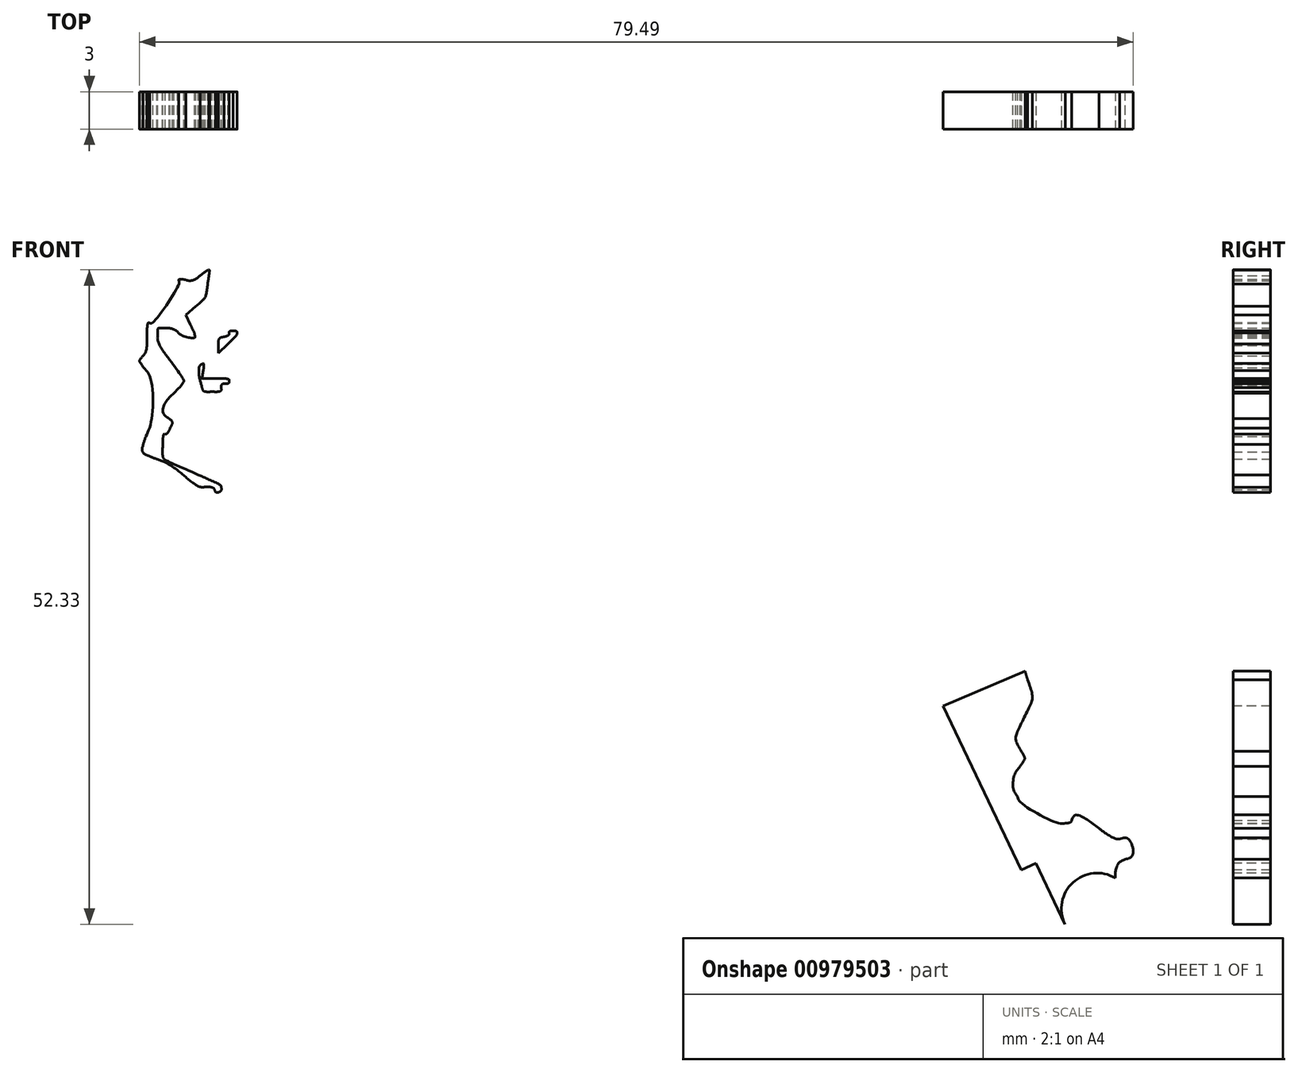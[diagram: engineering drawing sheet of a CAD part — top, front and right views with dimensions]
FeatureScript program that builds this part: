
annotation { "Feature Type Name" : "Feature", "Feature Type Description" : "" }
export const myFeature = defineFeature(function(context is Context, id is Id, definition is map)
    precondition{}
    {
        {
            var Q0;
            Q0=qCreatedBy(makeId("Front.planeOp"),FACE);
            var sketch = newSketch(context, id + "F0", { "sketchPlane" : qUnion([Q0])});
            skLineSegment(sketch, "E0", {"start": v(-32.88, 19.2) * mm, "end": v(-32.1, 20.83) * mm});
            skLineSegment(sketch, "E1", {"start": v(-32.1, 20.83) * mm, "end": v(-32.57, 22.16) * mm});
            skLineSegment(sketch, "E2", {"start": v(-27.5, 16.63) * mm, "end": v(-26.83, 16.28) * mm});
            skLineSegment(sketch, "E3", {"start": v(-26.83, 16.28) * mm, "end": v(-26.97, 16.83) * mm});
            skLineSegment(sketch, "E4", {"start": v(-24.85, 15.67) * mm, "end": v(-25.4, 15.88) * mm});
            skLineSegment(sketch, "E5", {"start": v(-25.4, 15.88) * mm, "end": v(-25.34, 18.4) * mm});
            skLineSegment(sketch, "E6", {"start": v(-1.75, 78.04) * mm, "end": v(-0.2, 79.6) * mm});
            skLineSegment(sketch, "E7", {"start": v(-0.2, 79.6) * mm, "end": v(1.27, 79.6) * mm});
            skLineSegment(sketch, "E8", {"start": v(38.3, 44.26) * mm, "end": v(38.3, 43.17) * mm});
            skLineSegment(sketch, "E9", {"start": v(38.3, 43.17) * mm, "end": v(37.62, 43.24) * mm});
            skLineSegment(sketch, "E10", {"start": v(39.65, -31.25) * mm, "end": v(39.52, -33.83) * mm});
            skLineSegment(sketch, "E11", {"start": v(39.52, -33.83) * mm, "end": v(40.18, -34.42) * mm});
            skLineSegment(sketch, "E12", {"start": v(1.4, 79.08) * mm, "end": v(0.3, 79.22) * mm});
            skLineSegment(sketch, "E13", {"start": v(0.3, 79.22) * mm, "end": v(-1.23, 77.67) * mm});
            skLineSegment(sketch, "E14", {"start": v(-12.51, 69.45) * mm, "end": v(-13.4, 69.45) * mm});
            skLineSegment(sketch, "E15", {"start": v(-13.4, 69.45) * mm, "end": v(-13.27, 67.07) * mm});
            skLineSegment(sketch, "E16", {"start": v(-18.31, 54.9) * mm, "end": v(-18.88, 53.48) * mm});
            skLineSegment(sketch, "E17", {"start": v(-18.88, 53.48) * mm, "end": v(-18.43, 53.1) * mm});
            skLineSegment(sketch, "E18", {"start": v(-20.94, 40.45) * mm, "end": v(-21.55, 40.45) * mm});
            skLineSegment(sketch, "E19", {"start": v(-21.55, 40.45) * mm, "end": v(-21.44, 41.8) * mm});
            skLineSegment(sketch, "E20", {"start": v(-24.47, 43.3) * mm, "end": v(-25.23, 42.61) * mm});
            skLineSegment(sketch, "E21", {"start": v(-25.23, 42.61) * mm, "end": v(-24.8, 41.05) * mm});
            skLineSegment(sketch, "E22", {"start": v(-37.96, -16.18) * mm, "end": v(-37.29, -17.23) * mm});
            skLineSegment(sketch, "E23", {"start": v(-37.29, -17.23) * mm, "end": v(-37.41, -20.41) * mm});
            skLineSegment(sketch, "E24", {"start": v(-30.4, -60.92) * mm, "end": v(-31.42, -62.04) * mm});
            skLineSegment(sketch, "E25", {"start": v(-31.42, -62.04) * mm, "end": v(-30.9, -63.02) * mm});
            skLineSegment(sketch, "E26", {"start": v(-36.35, 33.14) * mm, "end": v(-36.7, 33.88) * mm});
            skLineSegment(sketch, "E27", {"start": v(-36.7, 33.88) * mm, "end": v(-35.92, 34.57) * mm});
            skLineSegment(sketch, "E28", {"start": v(-34.09, 31.43) * mm, "end": v(-34.09, 30.84) * mm});
            skLineSegment(sketch, "E29", {"start": v(-34.09, 30.84) * mm, "end": v(-33.35, 31.56) * mm});
            skFitSpline(sketch, "E30", {"points": [v(-13.45, -80.7) * mm, v(-14.26, -80.4) * mm, v(-15.79, -79.86) * mm, v(-16.84, -79.51) * mm]});
            skFitSpline(sketch, "E31", {"points": [v(-16.84, -79.51) * mm, v(-20.43, -78.33) * mm, v(-20.6, -78.25) * mm, v(-21.55, -77.26) * mm]});
            skFitSpline(sketch, "E32", {"points": [v(-21.55, -77.26) * mm, v(-22.07, -76.72) * mm, v(-23.66, -74.52) * mm, v(-25.09, -72.37) * mm]});
            skFitSpline(sketch, "E33", {"points": [v(-25.09, -72.37) * mm, v(-26.52, -70.21) * mm, v(-28.36, -67.6) * mm, v(-29.19, -66.55) * mm]});
            skFitSpline(sketch, "E34", {"points": [v(-29.19, -66.55) * mm, v(-30.6, -64.76) * mm, v(-31.97, -62.53) * mm, v(-31.97, -62.03) * mm]});
            skFitSpline(sketch, "E35", {"points": [v(-31.97, -62.03) * mm, v(-31.97, -61.91) * mm, v(-31.5, -61.27) * mm, v(-30.92, -60.6) * mm]});
            skFitSpline(sketch, "E36", {"points": [v(-30.92, -60.6) * mm, v(-29.85, -59.39) * mm, v(-29, -57.92) * mm, v(-29, -57.28) * mm]});
            skFitSpline(sketch, "E37", {"points": [v(-29, -57.28) * mm, v(-29, -57.08) * mm, v(-29.34, -56.3) * mm, v(-29.75, -55.53) * mm]});
            skFitSpline(sketch, "E38", {"points": [v(-29.75, -55.53) * mm, v(-30.57, -53.98) * mm, v(-30.63, -53.57) * mm, v(-30.2, -52.72) * mm]});
            skFitSpline(sketch, "E39", {"points": [v(-30.2, -52.72) * mm, v(-29.95, -52.26) * mm, v(-29.92, -51.55) * mm, v(-30.04, -49.29) * mm]});
            skFitSpline(sketch, "E40", {"points": [v(-30.04, -49.29) * mm, v(-30.2, -46.13) * mm, v(-30.12, -46.32) * mm, v(-32.34, -43.6) * mm]});
            skFitSpline(sketch, "E41", {"points": [v(-32.34, -43.6) * mm, v(-32.83, -43) * mm, v(-33.38, -42.01) * mm, v(-33.55, -41.42) * mm]});
            skFitSpline(sketch, "E42", {"points": [v(-33.55, -41.42) * mm, v(-33.73, -40.84) * mm, v(-34.2, -39.94) * mm, v(-34.62, -39.44) * mm]});
            skFitSpline(sketch, "E43", {"points": [v(-34.62, -39.44) * mm, v(-36.03, -37.71) * mm, v(-36.52, -35.97) * mm, v(-35.98, -34.56) * mm]});
            skFitSpline(sketch, "E44", {"points": [v(-35.98, -34.56) * mm, v(-35.86, -34.24) * mm, v(-35.38, -33.57) * mm, v(-34.92, -33.07) * mm]});
            skFitSpline(sketch, "E45", {"points": [v(-34.92, -33.07) * mm, v(-33.97, -32.03) * mm, v(-34, -32.17) * mm, v(-34.37, -30.78) * mm]});
            skFitSpline(sketch, "E46", {"points": [v(-34.37, -30.78) * mm, v(-34.75, -29.38) * mm, v(-35.2, -28.53) * mm, v(-36.46, -26.88) * mm]});
            skFitSpline(sketch, "E47", {"points": [v(-36.46, -26.88) * mm, v(-37.04, -26.13) * mm, v(-37.61, -25.27) * mm, v(-37.73, -24.97) * mm]});
            skFitSpline(sketch, "E48", {"points": [v(-37.73, -24.97) * mm, v(-37.97, -24.39) * mm, v(-38.06, -21.07) * mm, v(-37.9, -18.8) * mm]});
            skFitSpline(sketch, "E49", {"points": [v(-37.9, -18.8) * mm, v(-37.82, -17.55) * mm, v(-37.87, -17.35) * mm, v(-38.39, -16.67) * mm]});
            skFitSpline(sketch, "E50", {"points": [v(-38.39, -16.67) * mm, v(-39.51, -15.19) * mm, v(-39.6, -12.77) * mm, v(-38.72, -7.81) * mm]});
            skFitSpline(sketch, "E51", {"points": [v(-38.72, -7.81) * mm, v(-38.24, -5.14) * mm, v(-38.31, -2.1) * mm, v(-38.87, -1) * mm]});
            skFitSpline(sketch, "E52", {"points": [v(-38.87, -1) * mm, v(-39.1, -0.56) * mm, v(-39.11, -0.29) * mm, v(-38.94, 0.17) * mm]});
            skFitSpline(sketch, "E53", {"points": [v(-38.94, 0.17) * mm, v(-38.62, 1) * mm, v(-38.87, 3.38) * mm, v(-39.5, 5.38) * mm]});
            skFitSpline(sketch, "E54", {"points": [v(-39.5, 5.38) * mm, v(-39.78, 6.29) * mm, v(-40.01, 7.26) * mm, v(-40.01, 7.54) * mm]});
            skFitSpline(sketch, "E55", {"points": [v(-40.01, 7.54) * mm, v(-40.01, 7.83) * mm, v(-39.68, 9.05) * mm, v(-39.27, 10.27) * mm]});
            skFitSpline(sketch, "E56", {"points": [v(-39.27, 10.27) * mm, v(-38.41, 12.85) * mm, v(-38.39, 13.06) * mm, v(-38.96, 13.2) * mm]});
            skFitSpline(sketch, "E57", {"points": [v(-38.96, 13.2) * mm, v(-39.71, 13.4) * mm, v(-39.48, 14.32) * mm, v(-38.38, 15.5) * mm]});
            skFitSpline(sketch, "E58", {"points": [v(-38.38, 15.5) * mm, v(-36.83, 17.16) * mm, v(-35.68, 17.57) * mm, v(-34.74, 16.8) * mm]});
            skFitSpline(sketch, "E59", {"points": [v(-34.74, 16.8) * mm, v(-34.08, 16.26) * mm, v(-32.77, 13.22) * mm, v(-32.66, 11.98) * mm]});
            skFitSpline(sketch, "E60", {"points": [v(-32.66, 11.98) * mm, v(-32.55, 10.86) * mm, v(-32.37, 10.61) * mm, v(-31.6, 10.6) * mm]});
            skFitSpline(sketch, "E61", {"points": [v(-31.6, 10.6) * mm, v(-31, 10.6) * mm, v(-30.96, 11.24) * mm, v(-31.55, 11.77) * mm]});
            skFitSpline(sketch, "E62", {"points": [v(-31.55, 11.77) * mm, v(-31.84, 12.03) * mm, v(-31.97, 12.42) * mm, v(-31.97, 13) * mm]});
            skFitSpline(sketch, "E63", {"points": [v(-31.97, 13) * mm, v(-31.97, 14.32) * mm, v(-32.62, 16.12) * mm, v(-33.18, 16.38) * mm]});
            skFitSpline(sketch, "E64", {"points": [v(-33.18, 16.38) * mm, v(-33.86, 16.69) * mm, v(-33.8, 17.27) * mm, v(-32.88, 19.2) * mm]});
            skFitSpline(sketch, "E65", {"points": [v(-32.57, 22.16) * mm, v(-32.82, 22.9) * mm, v(-33.03, 23.65) * mm, v(-33.03, 23.83) * mm]});
            skFitSpline(sketch, "E66", {"points": [v(-33.03, 23.83) * mm, v(-33.03, 24.1) * mm, v(-33.14, 24.14) * mm, v(-33.5, 24.01) * mm]});
            skFitSpline(sketch, "E67", {"points": [v(-33.5, 24.01) * mm, v(-33.77, 23.92) * mm, v(-34.4, 23.84) * mm, v(-34.93, 23.84) * mm]});
            skFitSpline(sketch, "E68", {"points": [v(-34.93, 23.84) * mm, v(-35.84, 23.83) * mm, v(-35.89, 23.86) * mm, v(-35.95, 24.48) * mm]});
            skFitSpline(sketch, "E69", {"points": [v(-35.95, 24.48) * mm, v(-36.05, 25.55) * mm, v(-34.78, 26.27) * mm, v(-32.78, 26.27) * mm]});
            skFitSpline(sketch, "E70", {"points": [v(-32.78, 26.27) * mm, v(-31.93, 26.27) * mm, v(-31.64, 26.16) * mm, v(-31.1, 25.65) * mm]});
            skFitSpline(sketch, "E71", {"points": [v(-31.1, 25.65) * mm, v(-30.75, 25.3) * mm, v(-30.32, 25.08) * mm, v(-30.15, 25.14) * mm]});
            skFitSpline(sketch, "E72", {"points": [v(-30.15, 25.14) * mm, v(-29.7, 25.31) * mm, v(-29.77, 25.47) * mm, v(-30.7, 26.37) * mm]});
            skFitSpline(sketch, "E73", {"points": [v(-30.7, 26.37) * mm, v(-31.5, 27.15) * mm, v(-31.55, 27.27) * mm, v(-31.55, 28.43) * mm]});
            skFitSpline(sketch, "E74", {"points": [v(-31.55, 28.43) * mm, v(-31.55, 29.6) * mm, v(-31.52, 29.65) * mm, v(-31.02, 29.65) * mm]});
            skFitSpline(sketch, "E75", {"points": [v(-31.02, 29.65) * mm, v(-30.7, 29.65) * mm, v(-30.49, 29.53) * mm, v(-30.49, 29.36) * mm]});
            skFitSpline(sketch, "E76", {"points": [v(-30.49, 29.36) * mm, v(-30.49, 28.94) * mm, v(-28.82, 27.75) * mm, v(-28.24, 27.75) * mm]});
            skFitSpline(sketch, "E77", {"points": [v(-28.24, 27.75) * mm, v(-27.83, 27.75) * mm, v(-27.75, 27.6) * mm, v(-27.62, 26.6) * mm]});
            skFitSpline(sketch, "E78", {"points": [v(-27.62, 26.6) * mm, v(-27.46, 25.26) * mm, v(-27.66, 24.55) * mm, v(-28.57, 23.22) * mm]});
            skFitSpline(sketch, "E79", {"points": [v(-28.57, 23.22) * mm, v(-29.21, 22.29) * mm, v(-29.4, 21.61) * mm, v(-29.02, 21.61) * mm]});
            skFitSpline(sketch, "E80", {"points": [v(-29.02, 21.61) * mm, v(-28.66, 21.61) * mm, v(-28.35, 20.18) * mm, v(-28.49, 19.14) * mm]});
            skFitSpline(sketch, "E81", {"points": [v(-28.49, 19.14) * mm, v(-28.66, 17.84) * mm, v(-28.36, 17.07) * mm, v(-27.5, 16.63) * mm]});
            skFitSpline(sketch, "E82", {"points": [v(-26.97, 16.83) * mm, v(-27.1, 17.33) * mm, v(-27.05, 17.38) * mm, v(-26.5, 17.38) * mm]});
            skFitSpline(sketch, "E83", {"points": [v(-26.5, 17.38) * mm, v(-25.81, 17.38) * mm, v(-25.62, 17.08) * mm, v(-25.62, 16.04) * mm]});
            skFitSpline(sketch, "E84", {"points": [v(-25.62, 16.04) * mm, v(-25.62, 15.5) * mm, v(-25.82, 15.19) * mm, v(-26.56, 14.52) * mm]});
            skFitSpline(sketch, "E85", {"points": [v(-26.56, 14.52) * mm, v(-27.09, 14.05) * mm, v(-27.58, 13.4) * mm, v(-27.66, 13.06) * mm]});
            skFitSpline(sketch, "E86", {"points": [v(-27.66, 13.06) * mm, v(-27.79, 12.49) * mm, v(-27.76, 12.45) * mm, v(-27.3, 12.58) * mm]});
            skFitSpline(sketch, "E87", {"points": [v(-27.3, 12.58) * mm, v(-27.01, 12.65) * mm, v(-26.47, 12.72) * mm, v(-26.09, 12.72) * mm]});
            skFitSpline(sketch, "E88", {"points": [v(-26.09, 12.72) * mm, v(-25.47, 12.72) * mm, v(-25.42, 12.76) * mm, v(-25.61, 13.13) * mm]});
            skFitSpline(sketch, "E89", {"points": [v(-25.61, 13.13) * mm, v(-26.02, 13.88) * mm, v(-25.88, 14.6) * mm, v(-25.31, 14.75) * mm]});
            skFitSpline(sketch, "E90", {"points": [v(-25.31, 14.75) * mm, v(-25.03, 14.82) * mm, v(-24.68, 15.01) * mm, v(-24.55, 15.17) * mm]});
            skFitSpline(sketch, "E91", {"points": [v(-24.55, 15.17) * mm, v(-24.35, 15.4) * mm, v(-24.42, 15.5) * mm, v(-24.85, 15.67) * mm]});
            skFitSpline(sketch, "E92", {"points": [v(-25.34, 18.4) * mm, v(-25.28, 20.49) * mm, v(-25.2, 21.05) * mm, v(-24.84, 21.66) * mm]});
            skFitSpline(sketch, "E93", {"points": [v(-24.84, 21.66) * mm, v(-24.6, 22.07) * mm, v(-24.33, 22.91) * mm, v(-24.25, 23.54) * mm]});
            skFitSpline(sketch, "E94", {"points": [v(-24.25, 23.54) * mm, v(-24.05, 24.98) * mm, v(-23.67, 25.42) * mm, v(-22.64, 25.42) * mm]});
            skFitSpline(sketch, "E95", {"points": [v(-22.64, 25.42) * mm, v(-21.97, 25.42) * mm, v(-21.73, 25.28) * mm, v(-21.09, 24.54) * mm]});
            skFitSpline(sketch, "E96", {"points": [v(-21.09, 24.54) * mm, v(-20.67, 24.05) * mm, v(-20.32, 23.55) * mm, v(-20.32, 23.43) * mm]});
            skFitSpline(sketch, "E97", {"points": [v(-20.32, 23.43) * mm, v(-20.3, 22.93) * mm, v(-19.5, 25.15) * mm, v(-19.5, 25.74) * mm]});
            skFitSpline(sketch, "E98", {"points": [v(-19.5, 25.74) * mm, v(-19.48, 26.68) * mm, v(-19.75, 27) * mm, v(-20.27, 26.68) * mm]});
            skFitSpline(sketch, "E99", {"points": [v(-20.27, 26.68) * mm, v(-20.84, 26.32) * mm, v(-23.7, 26.75) * mm, v(-24.99, 27.38) * mm]});
            skFitSpline(sketch, "E100", {"points": [v(-24.99, 27.38) * mm, v(-26.7, 28.23) * mm, v(-27.27, 29.95) * mm, v(-26.55, 32.07) * mm]});
            skFitSpline(sketch, "E101", {"points": [v(-26.55, 32.07) * mm, v(-26.23, 33) * mm, v(-26.23, 33.13) * mm, v(-26.58, 33.9) * mm]});
            skFitSpline(sketch, "E102", {"points": [v(-26.58, 33.9) * mm, v(-27.04, 34.91) * mm, v(-26.9, 36) * mm, v(-26.2, 36.92) * mm]});
            skFitSpline(sketch, "E103", {"points": [v(-26.2, 36.92) * mm, v(-24.96, 38.54) * mm, v(-24.76, 39.42) * mm, v(-25.3, 40.73) * mm]});
            skFitSpline(sketch, "E104", {"points": [v(-25.3, 40.73) * mm, v(-25.48, 41.15) * mm, v(-25.62, 41.87) * mm, v(-25.62, 42.33) * mm]});
            skFitSpline(sketch, "E105", {"points": [v(-25.62, 42.33) * mm, v(-25.62, 43.02) * mm, v(-25.5, 43.25) * mm, v(-24.99, 43.62) * mm]});
            skFitSpline(sketch, "E106", {"points": [v(-24.99, 43.62) * mm, v(-24.64, 43.87) * mm, v(-24.35, 44.26) * mm, v(-24.35, 44.48) * mm]});
            skFitSpline(sketch, "E107", {"points": [v(-24.35, 44.48) * mm, v(-24.35, 45.6) * mm, v(-22.43, 46.16) * mm, v(-21.62, 45.29) * mm]});
            skFitSpline(sketch, "E108", {"points": [v(-21.62, 45.29) * mm, v(-21.1, 44.74) * mm, v(-20.66, 42.78) * mm, v(-20.82, 41.8) * mm]});
            skFitSpline(sketch, "E109", {"points": [v(-20.82, 41.8) * mm, v(-20.95, 40.98) * mm, v(-20.5, 40.8) * mm, v(-20.12, 41.5) * mm]});
            skFitSpline(sketch, "E110", {"points": [v(-20.12, 41.5) * mm, v(-20, 41.74) * mm, v(-19.7, 41.93) * mm, v(-19.48, 41.93) * mm]});
            skFitSpline(sketch, "E111", {"points": [v(-19.48, 41.93) * mm, v(-19.2, 41.93) * mm, v(-19.03, 42.12) * mm, v(-18.95, 42.51) * mm]});
            skFitSpline(sketch, "E112", {"points": [v(-18.95, 42.51) * mm, v(-18.9, 42.83) * mm, v(-18.75, 43.5) * mm, v(-18.63, 44) * mm]});
            skFitSpline(sketch, "E113", {"points": [v(-18.63, 44) * mm, v(-18.15, 46.1) * mm, v(-18.46, 46.83) * mm, v(-19.95, 47.1) * mm]});
            skFitSpline(sketch, "E114", {"points": [v(-19.95, 47.1) * mm, v(-21.37, 47.35) * mm, v(-21.68, 48.31) * mm, v(-21.02, 50.45) * mm]});
            skFitSpline(sketch, "E115", {"points": [v(-21.02, 50.45) * mm, v(-20.67, 51.58) * mm, v(-20.6, 51.66) * mm, v(-20, 51.67) * mm]});
            skFitSpline(sketch, "E116", {"points": [v(-20, 51.67) * mm, v(-19.64, 51.67) * mm, v(-19.17, 51.8) * mm, v(-18.94, 51.97) * mm]});
            skFitSpline(sketch, "E117", {"points": [v(-18.94, 51.97) * mm, v(-18.56, 52.25) * mm, v(-18.55, 52.28) * mm, v(-18.9, 52.67) * mm]});
            skFitSpline(sketch, "E118", {"points": [v(-18.9, 52.67) * mm, v(-19.36, 53.18) * mm, v(-19.37, 53.99) * mm, v(-18.93, 55) * mm]});
            skFitSpline(sketch, "E119", {"points": [v(-18.93, 55) * mm, v(-18.26, 56.57) * mm, v(-18.22, 56.96) * mm, v(-18.55, 58.71) * mm]});
            skFitSpline(sketch, "E120", {"points": [v(-18.55, 58.71) * mm, v(-19.05, 61.35) * mm, v(-18.66, 63.1) * mm, v(-17.57, 63.1) * mm]});
            skFitSpline(sketch, "E121", {"points": [v(-17.57, 63.1) * mm, v(-17.13, 63.1) * mm, v(-16.93, 62.86) * mm, v(-16.62, 61.94) * mm]});
            skFitSpline(sketch, "E122", {"points": [v(-16.62, 61.94) * mm, v(-16.19, 60.62) * mm, v(-15.25, 61.36) * mm, v(-15.25, 63.03) * mm]});
            skFitSpline(sketch, "E123", {"points": [v(-15.25, 63.03) * mm, v(-15.25, 63.72) * mm, v(-15.21, 63.77) * mm, v(-14.72, 63.65) * mm]});
            skFitSpline(sketch, "E124", {"points": [v(-14.72, 63.65) * mm, v(-13.88, 63.44) * mm, v(-13.7, 64.21) * mm, v(-13.86, 67.25) * mm]});
            skFitSpline(sketch, "E125", {"points": [v(-13.86, 67.25) * mm, v(-14.01, 70.15) * mm, v(-14.06, 70.07) * mm, v(-12.21, 70.08) * mm]});
            skFitSpline(sketch, "E126", {"points": [v(-12.21, 70.08) * mm, v(-11.52, 70.08) * mm, v(-11.25, 70.23) * mm, v(-10.4, 71.12) * mm]});
            skFitSpline(sketch, "E127", {"points": [v(-10.4, 71.12) * mm, v(-9.38, 72.18) * mm, v(-9.03, 72.34) * mm, v(-6.52, 72.84) * mm]});
            skFitSpline(sketch, "E128", {"points": [v(-6.52, 72.84) * mm, v(-4.93, 73.15) * mm, v(-4.21, 73.78) * mm, v(-3.7, 75.27) * mm]});
            skFitSpline(sketch, "E129", {"points": [v(-3.7, 75.27) * mm, v(-3.38, 76.2) * mm, v(-2.96, 76.8) * mm, v(-1.75, 78.04) * mm]});
            skFitSpline(sketch, "E130", {"points": [v(1.27, 79.6) * mm, v(2.66, 79.6) * mm, v(2.79, 79.65) * mm, v(3.57, 80.36) * mm]});
            skFitSpline(sketch, "E131", {"points": [v(3.57, 80.36) * mm, v(4.72, 81.4) * mm, v(5.62, 81.51) * mm, v(6.84, 80.8) * mm]});
            skFitSpline(sketch, "E132", {"points": [v(6.84, 80.8) * mm, v(7.4, 80.48) * mm, v(8.11, 80.24) * mm, v(8.56, 80.24) * mm]});
            skFitSpline(sketch, "E133", {"points": [v(8.56, 80.24) * mm, v(9.65, 80.24) * mm, v(10.66, 79.76) * mm, v(12.03, 78.58) * mm]});
            skFitSpline(sketch, "E134", {"points": [v(12.03, 78.58) * mm, v(12.68, 78.02) * mm, v(13.76, 77.21) * mm, v(14.43, 76.8) * mm]});
            skFitSpline(sketch, "E135", {"points": [v(14.43, 76.8) * mm, v(16.07, 75.75) * mm, v(16.3, 75.23) * mm, v(16.26, 72.68) * mm]});
            skFitSpline(sketch, "E136", {"points": [v(16.26, 72.68) * mm, v(16.21, 70.3) * mm, v(16.3, 70.06) * mm, v(17.99, 67.97) * mm]});
            skFitSpline(sketch, "E137", {"points": [v(17.99, 67.97) * mm, v(19.34, 66.28) * mm, v(19.58, 65.73) * mm, v(19.78, 63.84) * mm]});
            skFitSpline(sketch, "E138", {"points": [v(19.78, 63.84) * mm, v(19.97, 61.97) * mm, v(20.1, 61.75) * mm, v(21.2, 61.28) * mm]});
            skFitSpline(sketch, "E139", {"points": [v(21.2, 61.28) * mm, v(21.95, 60.97) * mm, v(22.77, 60.9) * mm, v(25.95, 60.87) * mm]});
            skFitSpline(sketch, "E140", {"points": [v(25.95, 60.87) * mm, v(29.47, 60.83) * mm, v(29.87, 60.8) * mm, v(30.78, 60.35) * mm]});
            skFitSpline(sketch, "E141", {"points": [v(30.78, 60.35) * mm, v(31.33, 60.09) * mm, v(31.82, 59.71) * mm, v(31.88, 59.53) * mm]});
            skFitSpline(sketch, "E142", {"points": [v(31.88, 59.53) * mm, v(32.1, 58.78) * mm, v(32.32, 58.58) * mm, v(33.34, 58.19) * mm]});
            skFitSpline(sketch, "E143", {"points": [v(33.34, 58.19) * mm, v(35, 57.54) * mm, v(35.47, 56.96) * mm, v(35.61, 55.41) * mm]});
            skFitSpline(sketch, "E144", {"points": [v(35.61, 55.41) * mm, v(35.68, 54.7) * mm, v(35.93, 53.67) * mm, v(36.17, 53.15) * mm]});
            skFitSpline(sketch, "E145", {"points": [v(36.17, 53.15) * mm, v(36.4, 52.63) * mm, v(36.6, 51.94) * mm, v(36.6, 51.62) * mm]});
            skFitSpline(sketch, "E146", {"points": [v(36.6, 51.62) * mm, v(36.6, 51.3) * mm, v(36.8, 50.55) * mm, v(37.02, 49.93) * mm]});
            skFitSpline(sketch, "E147", {"points": [v(37.02, 49.93) * mm, v(37.7, 48.08) * mm, v(38.3, 45.42) * mm, v(38.3, 44.26) * mm]});
            skFitSpline(sketch, "E148", {"points": [v(37.62, 43.24) * mm, v(36.87, 43.31) * mm, v(36.86, 43.33) * mm, v(36.05, 46.9) * mm]});
            skFitSpline(sketch, "E149", {"points": [v(36.05, 46.9) * mm, v(35.75, 48.23) * mm, v(35.65, 48.45) * mm, v(35.6, 47.92) * mm]});
            skFitSpline(sketch, "E150", {"points": [v(35.6, 47.92) * mm, v(35.56, 47.55) * mm, v(35.72, 46.61) * mm, v(35.96, 45.84) * mm]});
            skFitSpline(sketch, "E151", {"points": [v(35.96, 45.84) * mm, v(36.2, 45.06) * mm, v(36.4, 44.16) * mm, v(36.4, 43.83) * mm]});
            skFitSpline(sketch, "E152", {"points": [v(36.4, 43.83) * mm, v(36.4, 42.72) * mm, v(36.23, 42.57) * mm, v(35.04, 42.57) * mm]});
            skFitSpline(sketch, "E153", {"points": [v(35.04, 42.57) * mm, v(34.35, 42.57) * mm, v(33.78, 42.44) * mm, v(33.53, 42.23) * mm]});
            skFitSpline(sketch, "E154", {"points": [v(33.53, 42.23) * mm, v(33.14, 41.92) * mm, v(33.15, 41.9) * mm, v(33.78, 42.01) * mm]});
            skFitSpline(sketch, "E155", {"points": [v(33.78, 42.01) * mm, v(34.37, 42.1) * mm, v(34.48, 42.05) * mm, v(34.7, 41.5) * mm]});
            skFitSpline(sketch, "E156", {"points": [v(34.7, 41.5) * mm, v(35.23, 40.23) * mm, v(34.46, 39.89) * mm, v(32.77, 40.66) * mm]});
            skFitSpline(sketch, "E157", {"points": [v(32.77, 40.66) * mm, v(30, 41.91) * mm, v(30.46, 40.26) * mm, v(33.3, 38.77) * mm]});
            skFitSpline(sketch, "E158", {"points": [v(33.3, 38.77) * mm, v(34.7, 38.04) * mm, v(35.03, 37.98) * mm, v(35.2, 38.44) * mm]});
            skFitSpline(sketch, "E159", {"points": [v(35.2, 38.44) * mm, v(35.4, 38.97) * mm, v(36.94, 38.86) * mm, v(37.34, 38.29) * mm]});
            skFitSpline(sketch, "E160", {"points": [v(37.34, 38.29) * mm, v(37.8, 37.64) * mm, v(37.75, 36.5) * mm, v(37.25, 35.69) * mm]});
            skFitSpline(sketch, "E161", {"points": [v(37.25, 35.69) * mm, v(37.01, 35.31) * mm, v(36.68, 34.6) * mm, v(36.5, 34.09) * mm]});
            skFitSpline(sketch, "E162", {"points": [v(36.5, 34.09) * mm, v(36.07, 32.87) * mm, v(35.62, 32.4) * mm, v(34.86, 32.4) * mm]});
            skFitSpline(sketch, "E163", {"points": [v(34.86, 32.4) * mm, v(34.06, 32.4) * mm, v(32.85, 32.98) * mm, v(32.57, 33.5) * mm]});
            skFitSpline(sketch, "E164", {"points": [v(32.57, 33.5) * mm, v(32.35, 33.9) * mm, v(32.37, 33.91) * mm, v(33.4, 34.23) * mm]});
            skFitSpline(sketch, "E165", {"points": [v(33.4, 34.23) * mm, v(33.55, 34.27) * mm, v(33.64, 34.43) * mm, v(33.6, 34.58) * mm]});
            skFitSpline(sketch, "E166", {"points": [v(33.6, 34.58) * mm, v(33.47, 34.97) * mm, v(32.1, 35.02) * mm, v(31.26, 34.66) * mm]});
            skFitSpline(sketch, "E167", {"points": [v(31.26, 34.66) * mm, v(30.63, 34.4) * mm, v(30.54, 34.27) * mm, v(30.63, 33.8) * mm]});
            skFitSpline(sketch, "E168", {"points": [v(30.63, 33.8) * mm, v(30.71, 33.37) * mm, v(30.83, 33.27) * mm, v(31.13, 33.37) * mm]});
            skFitSpline(sketch, "E169", {"points": [v(31.13, 33.37) * mm, v(31.68, 33.54) * mm, v(31.8, 33.13) * mm, v(31.57, 31.7) * mm]});
            skFitSpline(sketch, "E170", {"points": [v(31.57, 31.7) * mm, v(31.47, 31.04) * mm, v(31.4, 30.5) * mm, v(31.43, 30.5) * mm]});
            skFitSpline(sketch, "E171", {"points": [v(31.43, 30.5) * mm, v(31.46, 30.5) * mm, v(31.82, 30.65) * mm, v(32.25, 30.82) * mm]});
            skFitSpline(sketch, "E172", {"points": [v(32.25, 30.82) * mm, v(33.01, 31.14) * mm, v(33.02, 31.14) * mm, v(33.26, 30.56) * mm]});
            skFitSpline(sketch, "E173", {"points": [v(33.26, 30.56) * mm, v(33.39, 30.24) * mm, v(33.5, 29.43) * mm, v(33.52, 28.77) * mm]});
            skFitSpline(sketch, "E174", {"points": [v(33.52, 28.77) * mm, v(33.55, 27.14) * mm, v(33.03, 26.57) * mm, v(31.4, 26.43) * mm]});
            skFitSpline(sketch, "E175", {"points": [v(31.4, 26.43) * mm, v(29.99, 26.32) * mm, v(29.27, 25.83) * mm, v(28.59, 24.5) * mm]});
            skFitSpline(sketch, "E176", {"points": [v(28.59, 24.5) * mm, v(28.09, 23.52) * mm, v(28.09, 23.5) * mm, v(28.46, 22.8) * mm]});
            skFitSpline(sketch, "E177", {"points": [v(28.46, 22.8) * mm, v(29.02, 21.76) * mm, v(28.8, 20.5) * mm, v(27.76, 18.77) * mm]});
            skFitSpline(sketch, "E178", {"points": [v(27.76, 18.77) * mm, v(26.26, 16.28) * mm, v(26.34, 15.6) * mm, v(28.5, 12.89) * mm]});
            skFitSpline(sketch, "E179", {"points": [v(28.5, 12.89) * mm, v(30.07, 10.9) * mm, v(30.64, 9.85) * mm, v(31.32, 7.7) * mm]});
            skFitSpline(sketch, "E180", {"points": [v(31.32, 7.7) * mm, v(31.79, 6.2) * mm, v(31.8, 6.14) * mm, v(31.41, 5.73) * mm]});
            skFitSpline(sketch, "E181", {"points": [v(31.41, 5.73) * mm, v(31.08, 5.36) * mm, v(31.06, 5.2) * mm, v(31.28, 4.6) * mm]});
            skFitSpline(sketch, "E182", {"points": [v(31.28, 4.6) * mm, v(31.65, 3.58) * mm, v(31.59, 2.92) * mm, v(31, 1.59) * mm]});
            skFitSpline(sketch, "E183", {"points": [v(31, 1.59) * mm, v(30.4, 0.22) * mm, v(30.37, 0) * mm, v(30.73, -0.98) * mm]});
            skFitSpline(sketch, "E184", {"points": [v(30.73, -0.98) * mm, v(30.96, -1.6) * mm, v(30.93, -1.79) * mm, v(30.48, -2.62) * mm]});
            skFitSpline(sketch, "E185", {"points": [v(30.48, -2.62) * mm, v(29.76, -3.92) * mm, v(30.03, -4.4) * mm, v(31.97, -5.39) * mm]});
            skFitSpline(sketch, "E186", {"points": [v(31.97, -5.39) * mm, v(33.32, -6.07) * mm, v(33.55, -6.12) * mm, v(34.1, -5.9) * mm]});
            skFitSpline(sketch, "E187", {"points": [v(34.1, -5.9) * mm, v(34.89, -5.57) * mm, v(35.48, -5.74) * mm, v(36.67, -6.64) * mm]});
            skFitSpline(sketch, "E188", {"points": [v(36.67, -6.64) * mm, v(37.21, -7.06) * mm, v(37.94, -7.45) * mm, v(38.28, -7.52) * mm]});
            skFitSpline(sketch, "E189", {"points": [v(38.28, -7.52) * mm, v(38.74, -7.61) * mm, v(38.97, -7.82) * mm, v(39.14, -8.29) * mm]});
            skFitSpline(sketch, "E190", {"points": [v(39.14, -8.29) * mm, v(39.46, -9.22) * mm, v(39.43, -9.36) * mm, v(38.73, -10.24) * mm]});
            skFitSpline(sketch, "E191", {"points": [v(38.73, -10.24) * mm, v(37.95, -11.22) * mm, v(37.9, -12.13) * mm, v(38.57, -13.12) * mm]});
            skFitSpline(sketch, "E192", {"points": [v(38.57, -13.12) * mm, v(38.94, -13.67) * mm, v(39.23, -13.86) * mm, v(39.79, -13.91) * mm]});
            skFitSpline(sketch, "E193", {"points": [v(39.79, -13.91) * mm, v(40.2, -13.95) * mm, v(40.6, -14.1) * mm, v(40.68, -14.23) * mm]});
            skFitSpline(sketch, "E194", {"points": [v(40.68, -14.23) * mm, v(40.98, -14.7) * mm, v(40.84, -15.58) * mm, v(40.4, -15.98) * mm]});
            skFitSpline(sketch, "E195", {"points": [v(40.4, -15.98) * mm, v(40.04, -16.3) * mm, v(39.97, -16.56) * mm, v(40.05, -17.26) * mm]});
            skFitSpline(sketch, "E196", {"points": [v(40.05, -17.26) * mm, v(40.14, -18.03) * mm, v(40.09, -18.17) * mm, v(39.65, -18.37) * mm]});
            skFitSpline(sketch, "E197", {"points": [v(39.65, -18.37) * mm, v(39.06, -18.64) * mm, v(39.03, -18.9) * mm, v(39.5, -20) * mm]});
            skFitSpline(sketch, "E198", {"points": [v(39.5, -20) * mm, v(39.77, -20.67) * mm, v(39.83, -21.57) * mm, v(39.81, -24.74) * mm]});
            skFitSpline(sketch, "E199", {"points": [v(39.81, -24.74) * mm, v(39.8, -26.9) * mm, v(39.73, -29.82) * mm, v(39.65, -31.25) * mm]});
            skFitSpline(sketch, "E200", {"points": [v(40.18, -34.42) * mm, v(40.54, -34.74) * mm, v(40.84, -35.18) * mm, v(40.84, -35.41) * mm]});
            skFitSpline(sketch, "E201", {"points": [v(40.84, -35.41) * mm, v(40.84, -36.27) * mm, v(39.96, -37.65) * mm, v(38.92, -38.41) * mm]});
            skFitSpline(sketch, "E202", {"points": [v(38.92, -38.41) * mm, v(37.63, -39.36) * mm, v(37.28, -40) * mm, v(37.05, -41.89) * mm]});
            skFitSpline(sketch, "E203", {"points": [v(37.05, -41.89) * mm, v(36.94, -42.7) * mm, v(36.66, -43.77) * mm, v(36.42, -44.27) * mm]});
            skFitSpline(sketch, "E204", {"points": [v(36.42, -44.27) * mm, v(35.96, -45.22) * mm, v(33.78, -47.87) * mm, v(31.3, -50.5) * mm]});
            skFitSpline(sketch, "E205", {"points": [v(31.3, -50.5) * mm, v(29.02, -52.92) * mm, v(27.8, -55.66) * mm, v(27.2, -59.77) * mm]});
            skFitSpline(sketch, "E206", {"points": [v(27.2, -59.77) * mm, v(26.85, -62.13) * mm, v(26.75, -62.37) * mm, v(25.14, -65) * mm]});
            skFitSpline(sketch, "E207", {"points": [v(25.14, -65) * mm, v(24.58, -65.91) * mm, v(24.35, -66.6) * mm, v(24.16, -67.9) * mm]});
            skFitSpline(sketch, "E208", {"points": [v(24.16, -67.9) * mm, v(23.88, -69.93) * mm, v(23.36, -71.03) * mm, v(22.29, -71.92) * mm]});
            skFitSpline(sketch, "E209", {"points": [v(22.29, -71.92) * mm, v(21.43, -72.63) * mm, v(19.94, -73.22) * mm, v(19, -73.22) * mm]});
            skFitSpline(sketch, "E210", {"points": [v(19, -73.22) * mm, v(18.6, -73.22) * mm, v(18.4, -73.32) * mm, v(18.4, -73.56) * mm]});
            skFitSpline(sketch, "E211", {"points": [v(18.4, -73.56) * mm, v(18.4, -73.75) * mm, v(18.21, -74.22) * mm, v(17.97, -74.6) * mm]});
            skFitSpline(sketch, "E212", {"points": [v(17.97, -74.6) * mm, v(17.57, -75.26) * mm, v(17.56, -75.35) * mm, v(17.87, -76.08) * mm]});
            skFitSpline(sketch, "E213", {"points": [v(17.87, -76.08) * mm, v(18.34, -77.22) * mm, v(18.3, -77.38) * mm, v(17.14, -78.58) * mm]});
            skFitSpline(sketch, "E214", {"points": [v(17.14, -78.58) * mm, v(16.56, -79.18) * mm, v(15.87, -79.93) * mm, v(15.6, -80.25) * mm]});
            skFitSpline(sketch, "E215", {"points": [v(15.6, -80.25) * mm, v(15.34, -80.56) * mm, v(14.86, -80.88) * mm, v(14.54, -80.96) * mm]});
            skFitSpline(sketch, "E216", {"points": [v(14.54, -80.96) * mm, v(14.03, -81.08) * mm, v(13.96, -81.03) * mm, v(13.96, -80.56) * mm]});
            skFitSpline(sketch, "E217", {"points": [v(13.96, -80.56) * mm, v(13.96, -80.25) * mm, v(13.75, -79.86) * mm, v(13.47, -79.63) * mm]});
            skFitSpline(sketch, "E218", {"points": [v(13.47, -79.63) * mm, v(12.33, -78.73) * mm, v(12.3, -77.45) * mm, v(13.44, -77.45) * mm]});
            skFitSpline(sketch, "E219", {"points": [v(13.44, -77.45) * mm, v(14.2, -77.45) * mm, v(15.11, -76) * mm, v(14.94, -75.07) * mm]});
            skFitSpline(sketch, "E220", {"points": [v(14.94, -75.07) * mm, v(14.87, -74.7) * mm, v(14.75, -74.02) * mm, v(14.67, -73.57) * mm]});
            skFitSpline(sketch, "E221", {"points": [v(14.67, -73.57) * mm, v(14.58, -73.02) * mm, v(14.45, -72.8) * mm, v(14.25, -72.88) * mm]});
            skFitSpline(sketch, "E222", {"points": [v(14.25, -72.88) * mm, v(14.1, -72.94) * mm, v(13.13, -72.88) * mm, v(12.11, -72.76) * mm]});
            skFitSpline(sketch, "E223", {"points": [v(12.11, -72.76) * mm, v(10.8, -72.6) * mm, v(10.12, -72.4) * mm, v(9.8, -72.1) * mm]});
            skFitSpline(sketch, "E224", {"points": [v(9.8, -72.1) * mm, v(9.32, -71.67) * mm, v(8.88, -71.75) * mm, v(8.88, -72.28) * mm]});
            skFitSpline(sketch, "E225", {"points": [v(8.88, -72.28) * mm, v(8.88, -72.66) * mm, v(8.5, -72.65) * mm, v(7.82, -72.26) * mm]});
            skFitSpline(sketch, "E226", {"points": [v(7.82, -72.26) * mm, v(7.11, -71.86) * mm, v(5.83, -71.87) * mm, v(4.94, -72.29) * mm]});
            skFitSpline(sketch, "E227", {"points": [v(4.94, -72.29) * mm, v(4.16, -72.66) * mm, v(4.18, -72.61) * mm, v(4.14, -74.27) * mm]});
            skFitSpline(sketch, "E228", {"points": [v(4.14, -74.27) * mm, v(4.12, -75.43) * mm, v(4.11, -75.44) * mm, v(3.17, -75.91) * mm]});
            skFitSpline(sketch, "E229", {"points": [v(3.17, -75.91) * mm, v(2.65, -76.18) * mm, v(1.84, -76.77) * mm, v(1.36, -77.24) * mm]});
            skFitSpline(sketch, "E230", {"points": [v(1.36, -77.24) * mm, v(0.68, -77.91) * mm, v(-0.19, -78.37) * mm, v(-2.67, -79.37) * mm]});
            skFitSpline(sketch, "E231", {"points": [v(-2.67, -79.37) * mm, v(-6.5, -80.92) * mm, v(-7.82, -81.25) * mm, v(-10.17, -81.25) * mm]});
            skFitSpline(sketch, "E232", {"points": [v(-10.17, -81.25) * mm, v(-11.59, -81.25) * mm, v(-12.28, -81.13) * mm, v(-13.45, -80.7) * mm]});
            skFitSpline(sketch, "E233", {"points": [v(-6.84, -80.3) * mm, v(-6.29, -80.14) * mm, v(-4.56, -79.5) * mm, v(-3, -78.88) * mm]});
            skFitSpline(sketch, "E234", {"points": [v(-3, -78.88) * mm, v(-0.66, -77.96) * mm, v(0.05, -77.57) * mm, v(1.08, -76.65) * mm]});
            skFitSpline(sketch, "E235", {"points": [v(1.08, -76.65) * mm, v(1.77, -76.04) * mm, v(2.46, -75.54) * mm, v(2.62, -75.54) * mm]});
            skFitSpline(sketch, "E236", {"points": [v(2.62, -75.54) * mm, v(2.78, -75.54) * mm, v(3.12, -75.37) * mm, v(3.38, -75.16) * mm]});
            skFitSpline(sketch, "E237", {"points": [v(3.38, -75.16) * mm, v(3.8, -74.81) * mm, v(3.83, -74.72) * mm, v(3.59, -73.93) * mm]});
            skFitSpline(sketch, "E238", {"points": [v(3.59, -73.93) * mm, v(3.4, -73.28) * mm, v(3.39, -72.96) * mm, v(3.57, -72.61) * mm]});
            skFitSpline(sketch, "E239", {"points": [v(3.57, -72.61) * mm, v(4.07, -71.69) * mm, v(6.12, -71.11) * mm, v(7.53, -71.5) * mm]});
            skFitSpline(sketch, "E240", {"points": [v(7.53, -71.5) * mm, v(8.17, -71.68) * mm, v(8.4, -71.66) * mm, v(8.68, -71.41) * mm]});
            skFitSpline(sketch, "E241", {"points": [v(8.68, -71.41) * mm, v(9.15, -70.98) * mm, v(9.64, -71.02) * mm, v(10.13, -71.54) * mm]});
            skFitSpline(sketch, "E242", {"points": [v(10.13, -71.54) * mm, v(10.44, -71.88) * mm, v(10.95, -72.03) * mm, v(12.2, -72.17) * mm]});
            skFitSpline(sketch, "E243", {"points": [v(12.2, -72.17) * mm, v(13.1, -72.28) * mm, v(14, -72.32) * mm, v(14.17, -72.26) * mm]});
            skFitSpline(sketch, "E244", {"points": [v(14.17, -72.26) * mm, v(14.75, -72.09) * mm, v(15.04, -72.5) * mm, v(15.33, -73.91) * mm]});
            skFitSpline(sketch, "E245", {"points": [v(15.33, -73.91) * mm, v(15.54, -74.89) * mm, v(15.57, -75.53) * mm, v(15.43, -76.04) * mm]});
            skFitSpline(sketch, "E246", {"points": [v(15.43, -76.04) * mm, v(15.14, -77.06) * mm, v(14.45, -77.87) * mm, v(13.85, -77.87) * mm]});
            skFitSpline(sketch, "E247", {"points": [v(13.85, -77.87) * mm, v(13.06, -77.87) * mm, v(13.01, -78.27) * mm, v(13.7, -79) * mm]});
            skFitSpline(sketch, "E248", {"points": [v(13.7, -79) * mm, v(14.06, -79.37) * mm, v(14.38, -79.86) * mm, v(14.43, -80.1) * mm]});
            skFitSpline(sketch, "E249", {"points": [v(14.43, -80.1) * mm, v(14.5, -80.48) * mm, v(14.55, -80.47) * mm, v(15.03, -79.9) * mm]});
            skFitSpline(sketch, "E250", {"points": [v(15.03, -79.9) * mm, v(15.31, -79.57) * mm, v(16.02, -78.83) * mm, v(16.6, -78.28) * mm]});
            skFitSpline(sketch, "E251", {"points": [v(16.6, -78.28) * mm, v(17.64, -77.28) * mm, v(17.65, -77.26) * mm, v(17.4, -76.55) * mm]});
            skFitSpline(sketch, "E252", {"points": [v(17.4, -76.55) * mm, v(17.05, -75.6) * mm, v(17.07, -74.87) * mm, v(17.45, -74.37) * mm]});
            skFitSpline(sketch, "E253", {"points": [v(17.45, -74.37) * mm, v(17.62, -74.14) * mm, v(17.76, -73.7) * mm, v(17.76, -73.4) * mm]});
            skFitSpline(sketch, "E254", {"points": [v(17.76, -73.4) * mm, v(17.77, -72.89) * mm, v(17.86, -72.83) * mm, v(18.88, -72.7) * mm]});
            skFitSpline(sketch, "E255", {"points": [v(18.88, -72.7) * mm, v(19.5, -72.62) * mm, v(20.47, -72.3) * mm, v(21.04, -71.99) * mm]});
            skFitSpline(sketch, "E256", {"points": [v(21.04, -71.99) * mm, v(22.45, -71.22) * mm, v(23.22, -70.08) * mm, v(23.5, -68.35) * mm]});
            skFitSpline(sketch, "E257", {"points": [v(23.5, -68.35) * mm, v(23.9, -65.9) * mm, v(24.16, -65.2) * mm, v(25.1, -63.87) * mm]});
            skFitSpline(sketch, "E258", {"points": [v(25.1, -63.87) * mm, v(26.18, -62.33) * mm, v(26.35, -61.85) * mm, v(26.67, -59.46) * mm]});
            skFitSpline(sketch, "E259", {"points": [v(26.67, -59.46) * mm, v(26.98, -57.13) * mm, v(27.93, -54.18) * mm, v(28.89, -52.58) * mm]});
            skFitSpline(sketch, "E260", {"points": [v(28.89, -52.58) * mm, v(29.3, -51.88) * mm, v(30.25, -50.69) * mm, v(31, -49.93) * mm]});
            skFitSpline(sketch, "E261", {"points": [v(31, -49.93) * mm, v(33.26, -47.61) * mm, v(35.36, -45.01) * mm, v(35.9, -43.88) * mm]});
            skFitSpline(sketch, "E262", {"points": [v(35.9, -43.88) * mm, v(36.17, -43.28) * mm, v(36.49, -42.11) * mm, v(36.6, -41.27) * mm]});
            skFitSpline(sketch, "E263", {"points": [v(36.6, -41.27) * mm, v(36.81, -39.5) * mm, v(37.06, -39.06) * mm, v(38.37, -38.07) * mm]});
            skFitSpline(sketch, "E264", {"points": [v(38.37, -38.07) * mm, v(39.26, -37.4) * mm, v(40.2, -36.1) * mm, v(40.2, -35.57) * mm]});
            skFitSpline(sketch, "E265", {"points": [v(40.2, -35.57) * mm, v(40.2, -35.45) * mm, v(39.98, -35.11) * mm, v(39.7, -34.83) * mm]});
            skFitSpline(sketch, "E266", {"points": [v(39.7, -34.83) * mm, v(38.98, -34.12) * mm, v(38.86, -33.18) * mm, v(39.13, -30.68) * mm]});
            skFitSpline(sketch, "E267", {"points": [v(39.13, -30.68) * mm, v(39.26, -29.5) * mm, v(39.36, -26.93) * mm, v(39.36, -24.95) * mm]});
            skFitSpline(sketch, "E268", {"points": [v(39.36, -24.95) * mm, v(39.36, -21.87) * mm, v(39.3, -21.22) * mm, v(38.94, -20.3) * mm]});
            skFitSpline(sketch, "E269", {"points": [v(38.94, -20.3) * mm, v(38.39, -18.9) * mm, v(38.4, -18.51) * mm, v(39.04, -18) * mm]});
            skFitSpline(sketch, "E270", {"points": [v(39.04, -18) * mm, v(39.45, -17.69) * mm, v(39.57, -17.4) * mm, v(39.57, -16.76) * mm]});
            skFitSpline(sketch, "E271", {"points": [v(39.57, -16.76) * mm, v(39.57, -16.2) * mm, v(39.7, -15.8) * mm, v(39.97, -15.56) * mm]});
            skFitSpline(sketch, "E272", {"points": [v(39.97, -15.56) * mm, v(40.59, -15) * mm, v(40.32, -14.37) * mm, v(39.46, -14.37) * mm]});
            skFitSpline(sketch, "E273", {"points": [v(39.46, -14.37) * mm, v(38.38, -14.37) * mm, v(37.67, -13.4) * mm, v(37.67, -11.9) * mm]});
            skFitSpline(sketch, "E274", {"points": [v(37.67, -11.9) * mm, v(37.67, -10.72) * mm, v(37.93, -9.95) * mm, v(38.44, -9.65) * mm]});
            skFitSpline(sketch, "E275", {"points": [v(38.44, -9.65) * mm, v(39.04, -9.3) * mm, v(38.7, -8.02) * mm, v(38, -8.02) * mm]});
            skFitSpline(sketch, "E276", {"points": [v(38, -8.02) * mm, v(37.74, -8.02) * mm, v(37, -7.64) * mm, v(36.34, -7.18) * mm]});
            skFitSpline(sketch, "E277", {"points": [v(36.34, -7.18) * mm, v(35.18, -6.34) * mm, v(34.43, -6.12) * mm, v(34.18, -6.54) * mm]});
            skFitSpline(sketch, "E278", {"points": [v(34.18, -6.54) * mm, v(34.1, -6.66) * mm, v(33.87, -6.75) * mm, v(33.65, -6.75) * mm]});
            skFitSpline(sketch, "E279", {"points": [v(33.65, -6.75) * mm, v(33.07, -6.75) * mm, v(30.08, -5.09) * mm, v(29.83, -4.63) * mm]});
            skFitSpline(sketch, "E280", {"points": [v(29.83, -4.63) * mm, v(29.5, -4) * mm, v(29.6, -2.89) * mm, v(30.04, -2.22) * mm]});
            skFitSpline(sketch, "E281", {"points": [v(30.04, -2.22) * mm, v(30.4, -1.66) * mm, v(30.41, -1.54) * mm, v(30.14, -1.01) * mm]});
            skFitSpline(sketch, "E282", {"points": [v(30.14, -1.01) * mm, v(29.71, -0.19) * mm, v(29.76, 0.38) * mm, v(30.37, 1.68) * mm]});
            skFitSpline(sketch, "E283", {"points": [v(30.37, 1.68) * mm, v(30.96, 2.95) * mm, v(31, 3.5) * mm, v(30.65, 4.7) * mm]});
            skFitSpline(sketch, "E284", {"points": [v(30.65, 4.7) * mm, v(30.44, 5.4) * mm, v(30.46, 5.58) * mm, v(30.78, 5.93) * mm]});
            skFitSpline(sketch, "E285", {"points": [v(30.78, 5.93) * mm, v(31.13, 6.33) * mm, v(31.13, 6.4) * mm, v(30.68, 7.79) * mm]});
            skFitSpline(sketch, "E286", {"points": [v(30.68, 7.79) * mm, v(30.01, 9.8) * mm, v(29.64, 10.47) * mm, v(28.1, 12.43) * mm]});
            skFitSpline(sketch, "E287", {"points": [v(28.1, 12.43) * mm, v(27.35, 13.37) * mm, v(26.61, 14.44) * mm, v(26.46, 14.8) * mm]});
            skFitSpline(sketch, "E288", {"points": [v(26.46, 14.8) * mm, v(26, 15.95) * mm, v(26.28, 17.5) * mm, v(27.26, 19.16) * mm]});
            skFitSpline(sketch, "E289", {"points": [v(27.26, 19.16) * mm, v(28.4, 21.1) * mm, v(28.53, 21.7) * mm, v(27.93, 22.5) * mm]});
            skFitSpline(sketch, "E290", {"points": [v(27.93, 22.5) * mm, v(27.4, 23.23) * mm, v(27.46, 23.77) * mm, v(28.28, 25.17) * mm]});
            skFitSpline(sketch, "E291", {"points": [v(28.28, 25.17) * mm, v(28.94, 26.3) * mm, v(29.89, 26.9) * mm, v(31.02, 26.9) * mm]});
            skFitSpline(sketch, "E292", {"points": [v(31.02, 26.9) * mm, v(31.6, 26.9) * mm, v(32.1, 27.06) * mm, v(32.48, 27.36) * mm]});
            skFitSpline(sketch, "E293", {"points": [v(32.48, 27.36) * mm, v(33, 27.78) * mm, v(33.05, 27.91) * mm, v(32.96, 28.95) * mm]});
            skFitSpline(sketch, "E294", {"points": [v(32.96, 28.95) * mm, v(32.91, 29.57) * mm, v(32.82, 30.13) * mm, v(32.76, 30.19) * mm]});
            skFitSpline(sketch, "E295", {"points": [v(32.76, 30.19) * mm, v(32.7, 30.25) * mm, v(32.3, 30.15) * mm, v(31.89, 29.97) * mm]});
            skFitSpline(sketch, "E296", {"points": [v(31.89, 29.97) * mm, v(31.46, 29.8) * mm, v(31.06, 29.65) * mm, v(30.98, 29.65) * mm]});
            skFitSpline(sketch, "E297", {"points": [v(30.98, 29.65) * mm, v(30.9, 29.65) * mm, v(30.9, 30.37) * mm, v(30.97, 31.24) * mm]});
            skFitSpline(sketch, "E298", {"points": [v(30.97, 31.24) * mm, v(31.1, 32.73) * mm, v(31.07, 32.83) * mm, v(30.68, 32.83) * mm]});
            skFitSpline(sketch, "E299", {"points": [v(30.68, 32.83) * mm, v(30.45, 32.83) * mm, v(30.26, 32.97) * mm, v(30.26, 33.15) * mm]});
            skFitSpline(sketch, "E300", {"points": [v(30.26, 33.15) * mm, v(30.26, 33.32) * mm, v(30.16, 33.46) * mm, v(30.05, 33.46) * mm]});
            skFitSpline(sketch, "E301", {"points": [v(30.05, 33.46) * mm, v(29.69, 33.46) * mm, v(29.82, 34.44) * mm, v(30.23, 34.81) * mm]});
            skFitSpline(sketch, "E302", {"points": [v(30.23, 34.81) * mm, v(30.44, 35) * mm, v(31.16, 35.28) * mm, v(31.83, 35.42) * mm]});
            skFitSpline(sketch, "E303", {"points": [v(31.83, 35.42) * mm, v(32.85, 35.63) * mm, v(33.13, 35.62) * mm, v(33.6, 35.36) * mm]});
            skFitSpline(sketch, "E304", {"points": [v(33.6, 35.36) * mm, v(34.37, 34.93) * mm, v(34.48, 34.05) * mm, v(33.82, 33.73) * mm]});
            skFitSpline(sketch, "E305", {"points": [v(33.82, 33.73) * mm, v(33.34, 33.51) * mm, v(33.35, 33.5) * mm, v(34.15, 33.16) * mm]});
            skFitSpline(sketch, "E306", {"points": [v(34.15, 33.16) * mm, v(34.9, 32.83) * mm, v(34.99, 32.83) * mm, v(35.36, 33.17) * mm]});
            skFitSpline(sketch, "E307", {"points": [v(35.36, 33.17) * mm, v(35.58, 33.37) * mm, v(35.76, 33.64) * mm, v(35.76, 33.77) * mm]});
            skFitSpline(sketch, "E308", {"points": [v(35.76, 33.77) * mm, v(35.76, 33.9) * mm, v(36.1, 34.7) * mm, v(36.5, 35.56) * mm]});
            skFitSpline(sketch, "E309", {"points": [v(36.5, 35.56) * mm, v(37.29, 37.18) * mm, v(37.3, 37.75) * mm, v(36.61, 38.12) * mm]});
            skFitSpline(sketch, "E310", {"points": [v(36.61, 38.12) * mm, v(36.14, 38.38) * mm, v(35.55, 38.19) * mm, v(35.55, 37.78) * mm]});
            skFitSpline(sketch, "E311", {"points": [v(35.55, 37.78) * mm, v(35.55, 36.66) * mm, v(30.79, 39.12) * mm, v(30.36, 40.45) * mm]});
            skFitSpline(sketch, "E312", {"points": [v(30.36, 40.45) * mm, v(30.3, 40.68) * mm, v(30.34, 41.05) * mm, v(30.47, 41.29) * mm]});
            skFitSpline(sketch, "E313", {"points": [v(30.47, 41.29) * mm, v(30.77, 41.86) * mm, v(31.55, 41.83) * mm, v(33.01, 41.2) * mm]});
            skFitSpline(sketch, "E314", {"points": [v(33.01, 41.2) * mm, v(34.25, 40.67) * mm, v(34.4, 40.66) * mm, v(34.2, 41.18) * mm]});
            skFitSpline(sketch, "E315", {"points": [v(34.2, 41.18) * mm, v(34.13, 41.4) * mm, v(33.81, 41.5) * mm, v(33.34, 41.5) * mm]});
            skFitSpline(sketch, "E316", {"points": [v(33.34, 41.5) * mm, v(32.48, 41.5) * mm, v(32.37, 41.83) * mm, v(32.97, 42.57) * mm]});
            skFitSpline(sketch, "E317", {"points": [v(32.97, 42.57) * mm, v(33.3, 42.96) * mm, v(33.56, 43.04) * mm, v(34.54, 43.04) * mm]});
            skFitSpline(sketch, "E318", {"points": [v(34.54, 43.04) * mm, v(36.05, 43.02) * mm, v(36.12, 43.25) * mm, v(35.4, 45.67) * mm]});
            skFitSpline(sketch, "E319", {"points": [v(35.4, 45.67) * mm, v(34.98, 47.1) * mm, v(34.9, 47.7) * mm, v(35.01, 48.62) * mm]});
            skFitSpline(sketch, "E320", {"points": [v(35.01, 48.62) * mm, v(35.1, 49.37) * mm, v(35.26, 49.76) * mm, v(35.45, 49.76) * mm]});
            skFitSpline(sketch, "E321", {"points": [v(35.45, 49.76) * mm, v(35.79, 49.76) * mm, v(36.46, 48.04) * mm, v(36.81, 46.27) * mm]});
            skFitSpline(sketch, "E322", {"points": [v(36.81, 46.27) * mm, v(37.15, 44.53) * mm, v(37.45, 43.62) * mm, v(37.68, 43.62) * mm]});
            skFitSpline(sketch, "E323", {"points": [v(37.68, 43.62) * mm, v(37.8, 43.62) * mm, v(37.88, 43.84) * mm, v(37.88, 44.1) * mm]});
            skFitSpline(sketch, "E324", {"points": [v(37.88, 44.1) * mm, v(37.88, 44.74) * mm, v(36.88, 48.83) * mm, v(36.6, 49.36) * mm]});
            skFitSpline(sketch, "E325", {"points": [v(36.6, 49.36) * mm, v(36.47, 49.6) * mm, v(36.29, 50.3) * mm, v(36.19, 50.92) * mm]});
            skFitSpline(sketch, "E326", {"points": [v(36.19, 50.92) * mm, v(36.09, 51.54) * mm, v(35.8, 52.48) * mm, v(35.57, 53.01) * mm]});
            skFitSpline(sketch, "E327", {"points": [v(35.57, 53.01) * mm, v(35.31, 53.57) * mm, v(35.13, 54.41) * mm, v(35.13, 55.03) * mm]});
            skFitSpline(sketch, "E328", {"points": [v(35.13, 55.03) * mm, v(35.13, 56.37) * mm, v(34.52, 57.14) * mm, v(33.05, 57.66) * mm]});
            skFitSpline(sketch, "E329", {"points": [v(33.05, 57.66) * mm, v(31.97, 58.05) * mm, v(31.44, 58.5) * mm, v(31.02, 59.34) * mm]});
            skFitSpline(sketch, "E330", {"points": [v(31.02, 59.34) * mm, v(30.64, 60.08) * mm, v(29.4, 60.31) * mm, v(25.6, 60.34) * mm]});
            skFitSpline(sketch, "E331", {"points": [v(25.6, 60.34) * mm, v(21.36, 60.37) * mm, v(20.2, 60.66) * mm, v(19.62, 61.83) * mm]});
            skFitSpline(sketch, "E332", {"points": [v(19.62, 61.83) * mm, v(19.42, 62.24) * mm, v(19.25, 63.05) * mm, v(19.25, 63.63) * mm]});
            skFitSpline(sketch, "E333", {"points": [v(19.25, 63.63) * mm, v(19.24, 64.97) * mm, v(18.71, 66.14) * mm, v(17.39, 67.73) * mm]});
            skFitSpline(sketch, "E334", {"points": [v(17.39, 67.73) * mm, v(15.95, 69.45) * mm, v(15.56, 70.55) * mm, v(15.72, 72.4) * mm]});
            skFitSpline(sketch, "E335", {"points": [v(15.72, 72.4) * mm, v(15.89, 74.42) * mm, v(15.61, 75.26) * mm, v(14.57, 75.97) * mm]});
            skFitSpline(sketch, "E336", {"points": [v(14.57, 75.97) * mm, v(13.8, 76.48) * mm, v(12.94, 77.13) * mm, v(10.52, 78.96) * mm]});
            skFitSpline(sketch, "E337", {"points": [v(10.52, 78.96) * mm, v(9.93, 79.4) * mm, v(9.37, 79.6) * mm, v(8.4, 79.72) * mm]});
            skFitSpline(sketch, "E338", {"points": [v(8.4, 79.72) * mm, v(7.67, 79.8) * mm, v(6.83, 80.05) * mm, v(6.52, 80.27) * mm]});
            skFitSpline(sketch, "E339", {"points": [v(6.52, 80.27) * mm, v(5.73, 80.83) * mm, v(4.99, 80.76) * mm, v(4.18, 80.06) * mm]});
            skFitSpline(sketch, "E340", {"points": [v(4.18, 80.06) * mm, v(3.06, 79.09) * mm, v(2.62, 78.93) * mm, v(1.4, 79.08) * mm]});
            skFitSpline(sketch, "E341", {"points": [v(-1.23, 77.67) * mm, v(-2.35, 76.53) * mm, v(-2.88, 75.8) * mm, v(-3.2, 74.95) * mm]});
            skFitSpline(sketch, "E342", {"points": [v(-3.2, 74.95) * mm, v(-3.44, 74.31) * mm, v(-3.84, 73.58) * mm, v(-4.08, 73.32) * mm]});
            skFitSpline(sketch, "E343", {"points": [v(-4.08, 73.32) * mm, v(-4.6, 72.75) * mm, v(-5.86, 72.28) * mm, v(-7.31, 72.1) * mm]});
            skFitSpline(sketch, "E344", {"points": [v(-7.31, 72.1) * mm, v(-8.5, 71.94) * mm, v(-9.16, 71.58) * mm, v(-9.92, 70.68) * mm]});
            skFitSpline(sketch, "E345", {"points": [v(-9.92, 70.68) * mm, v(-10.62, 69.85) * mm, v(-11.46, 69.45) * mm, v(-12.51, 69.45) * mm]});
            skFitSpline(sketch, "E346", {"points": [v(-13.27, 67.07) * mm, v(-13.12, 64.4) * mm, v(-13.35, 63.34) * mm, v(-14.15, 63) * mm]});
            skFitSpline(sketch, "E347", {"points": [v(-14.15, 63) * mm, v(-14.41, 62.88) * mm, v(-14.68, 62.54) * mm, v(-14.74, 62.25) * mm]});
            skFitSpline(sketch, "E348", {"points": [v(-14.74, 62.25) * mm, v(-14.95, 61.27) * mm, v(-15.22, 60.8) * mm, v(-15.67, 60.66) * mm]});
            skFitSpline(sketch, "E349", {"points": [v(-15.67, 60.66) * mm, v(-16.3, 60.47) * mm, v(-17.15, 61.07) * mm, v(-17.15, 61.71) * mm]});
            skFitSpline(sketch, "E350", {"points": [v(-17.15, 61.71) * mm, v(-17.15, 62.4) * mm, v(-17.57, 62.62) * mm, v(-17.95, 62.12) * mm]});
            skFitSpline(sketch, "E351", {"points": [v(-17.95, 62.12) * mm, v(-18.25, 61.72) * mm, v(-18.24, 60.86) * mm, v(-17.87, 57.55) * mm]});
            skFitSpline(sketch, "E352", {"points": [v(-17.87, 57.55) * mm, v(-17.76, 56.53) * mm, v(-17.83, 56.11) * mm, v(-18.31, 54.9) * mm]});
            skFitSpline(sketch, "E353", {"points": [v(-18.43, 53.1) * mm, v(-18.09, 52.84) * mm, v(-18, 52.61) * mm, v(-18.12, 52.26) * mm]});
            skFitSpline(sketch, "E354", {"points": [v(-18.12, 52.26) * mm, v(-18.35, 51.5) * mm, v(-18.6, 51.29) * mm, v(-19.44, 51.14) * mm]});
            skFitSpline(sketch, "E355", {"points": [v(-19.44, 51.14) * mm, v(-20.16, 51.02) * mm, v(-20.25, 50.92) * mm, v(-20.59, 49.92) * mm]});
            skFitSpline(sketch, "E356", {"points": [v(-20.59, 49.92) * mm, v(-21.07, 48.49) * mm, v(-20.79, 47.82) * mm, v(-19.64, 47.63) * mm]});
            skFitSpline(sketch, "E357", {"points": [v(-19.64, 47.63) * mm, v(-18.7, 47.48) * mm, v(-18.1, 46.98) * mm, v(-17.9, 46.22) * mm]});
            skFitSpline(sketch, "E358", {"points": [v(-17.9, 46.22) * mm, v(-17.82, 45.92) * mm, v(-17.92, 44.77) * mm, v(-18.12, 43.68) * mm]});
            skFitSpline(sketch, "E359", {"points": [v(-18.12, 43.68) * mm, v(-18.44, 41.9) * mm, v(-18.54, 41.66) * mm, v(-19.03, 41.44) * mm]});
            skFitSpline(sketch, "E360", {"points": [v(-19.03, 41.44) * mm, v(-19.33, 41.3) * mm, v(-19.75, 41.02) * mm, v(-19.96, 40.82) * mm]});
            skFitSpline(sketch, "E361", {"points": [v(-19.96, 40.82) * mm, v(-20.16, 40.62) * mm, v(-20.6, 40.45) * mm, v(-20.94, 40.45) * mm]});
            skFitSpline(sketch, "E362", {"points": [v(-21.44, 41.8) * mm, v(-21.32, 43.27) * mm, v(-21.6, 44.43) * mm, v(-22.21, 44.98) * mm]});
            skFitSpline(sketch, "E363", {"points": [v(-22.21, 44.98) * mm, v(-22.54, 45.28) * mm, v(-22.7, 45.3) * mm, v(-23.16, 45.08) * mm]});
            skFitSpline(sketch, "E364", {"points": [v(-23.16, 45.08) * mm, v(-23.48, 44.93) * mm, v(-23.72, 44.65) * mm, v(-23.72, 44.41) * mm]});
            skFitSpline(sketch, "E365", {"points": [v(-23.72, 44.41) * mm, v(-23.72, 44.19) * mm, v(-24.06, 43.69) * mm, v(-24.47, 43.3) * mm]});
            skFitSpline(sketch, "E366", {"points": [v(-24.8, 41.05) * mm, v(-24.28, 39.2) * mm, v(-24.4, 38.43) * mm, v(-25.38, 37) * mm]});
            skFitSpline(sketch, "E367", {"points": [v(-25.38, 37) * mm, v(-26.38, 35.55) * mm, v(-26.52, 35.03) * mm, v(-26.15, 34.3) * mm]});
            skFitSpline(sketch, "E368", {"points": [v(-26.15, 34.3) * mm, v(-25.74, 33.52) * mm, v(-25.75, 32.64) * mm, v(-26.17, 31.34) * mm]});
            skFitSpline(sketch, "E369", {"points": [v(-26.17, 31.34) * mm, v(-26.5, 30.34) * mm, v(-26.5, 30.27) * mm, v(-26.05, 29.35) * mm]});
            skFitSpline(sketch, "E370", {"points": [v(-26.05, 29.35) * mm, v(-25.45, 28.12) * mm, v(-24.64, 27.64) * mm, v(-22.5, 27.27) * mm]});
            skFitSpline(sketch, "E371", {"points": [v(-22.5, 27.27) * mm, v(-21.03, 27.01) * mm, v(-20.71, 27.01) * mm, v(-20.51, 27.25) * mm]});
            skFitSpline(sketch, "E372", {"points": [v(-20.51, 27.25) * mm, v(-20.2, 27.62) * mm, v(-19.6, 27.62) * mm, v(-19.29, 27.24) * mm]});
            skFitSpline(sketch, "E373", {"points": [v(-19.29, 27.24) * mm, v(-18.74, 26.58) * mm, v(-18.77, 25.45) * mm, v(-19.37, 23.93) * mm]});
            skFitSpline(sketch, "E374", {"points": [v(-19.37, 23.93) * mm, v(-19.7, 23.08) * mm, v(-20.07, 22.46) * mm, v(-20.24, 22.46) * mm]});
            skFitSpline(sketch, "E375", {"points": [v(-20.24, 22.46) * mm, v(-20.4, 22.46) * mm, v(-20.54, 22.54) * mm, v(-20.54, 22.65) * mm]});
            skFitSpline(sketch, "E376", {"points": [v(-20.54, 22.65) * mm, v(-20.54, 23.08) * mm, v(-22.27, 25) * mm, v(-22.65, 25) * mm]});
            skFitSpline(sketch, "E377", {"points": [v(-22.65, 25) * mm, v(-23.23, 25) * mm, v(-23.72, 24.2) * mm, v(-23.72, 23.22) * mm]});
            skFitSpline(sketch, "E378", {"points": [v(-23.72, 23.22) * mm, v(-23.72, 22.72) * mm, v(-23.92, 22.04) * mm, v(-24.24, 21.5) * mm]});
            skFitSpline(sketch, "E379", {"points": [v(-24.24, 21.5) * mm, v(-24.66, 20.79) * mm, v(-24.75, 20.34) * mm, v(-24.74, 19.26) * mm]});
            skFitSpline(sketch, "E380", {"points": [v(-24.74, 19.26) * mm, v(-24.72, 18.51) * mm, v(-24.78, 17.69) * mm, v(-24.86, 17.43) * mm]});
            skFitSpline(sketch, "E381", {"points": [v(-24.86, 17.43) * mm, v(-25.08, 16.75) * mm, v(-24.82, 16.1) * mm, v(-24.33, 16.1) * mm]});
            skFitSpline(sketch, "E382", {"points": [v(-24.33, 16.1) * mm, v(-23.36, 16.1) * mm, v(-23.83, 14.55) * mm, v(-24.88, 14.3) * mm]});
            skFitSpline(sketch, "E383", {"points": [v(-24.88, 14.3) * mm, v(-25.3, 14.18) * mm, v(-25.36, 14.09) * mm, v(-25.2, 13.77) * mm]});
            skFitSpline(sketch, "E384", {"points": [v(-25.2, 13.77) * mm, v(-24.96, 13.34) * mm, v(-24.91, 12.23) * mm, v(-25.11, 12.03) * mm]});
            skFitSpline(sketch, "E385", {"points": [v(-25.11, 12.03) * mm, v(-25.18, 11.96) * mm, v(-25.46, 11.98) * mm, v(-25.73, 12.09) * mm]});
            skFitSpline(sketch, "E386", {"points": [v(-25.73, 12.09) * mm, v(-26.03, 12.2) * mm, v(-26.5, 12.18) * mm, v(-26.98, 12.04) * mm]});
            skFitSpline(sketch, "E387", {"points": [v(-26.98, 12.04) * mm, v(-28.78, 11.48) * mm, v(-28.79, 13.48) * mm, v(-26.99, 14.98) * mm]});
            skFitSpline(sketch, "E388", {"points": [v(-26.99, 14.98) * mm, v(-26.47, 15.42) * mm, v(-26.04, 15.92) * mm, v(-26.04, 16.09) * mm]});
            skFitSpline(sketch, "E389", {"points": [v(-26.04, 16.09) * mm, v(-26.04, 16.33) * mm, v(-26.1, 16.35) * mm, v(-26.3, 16.15) * mm]});
            skFitSpline(sketch, "E390", {"points": [v(-26.3, 16.15) * mm, v(-26.76, 15.69) * mm, v(-27.73, 15.86) * mm, v(-28.39, 16.52) * mm]});
            skFitSpline(sketch, "E391", {"points": [v(-28.39, 16.52) * mm, v(-28.98, 17.1) * mm, v(-29, 17.22) * mm, v(-29, 18.97) * mm]});
            skFitSpline(sketch, "E392", {"points": [v(-29, 18.97) * mm, v(-29, 20.63) * mm, v(-29.05, 20.82) * mm, v(-29.43, 20.91) * mm]});
            skFitSpline(sketch, "E393", {"points": [v(-29.43, 20.91) * mm, v(-30.19, 21.11) * mm, v(-29.94, 22.23) * mm, v(-28.69, 24.26) * mm]});
            skFitSpline(sketch, "E394", {"points": [v(-28.69, 24.26) * mm, v(-27.87, 25.58) * mm, v(-28, 27.33) * mm, v(-28.9, 27.33) * mm]});
            skFitSpline(sketch, "E395", {"points": [v(-28.9, 27.33) * mm, v(-29.17, 27.33) * mm, v(-29.7, 27.61) * mm, v(-30.07, 27.96) * mm]});
            skFitSpline(sketch, "E396", {"points": [v(-30.07, 27.96) * mm, v(-30.87, 28.71) * mm, v(-31.12, 28.76) * mm, v(-31.12, 28.14) * mm]});
            skFitSpline(sketch, "E397", {"points": [v(-31.12, 28.14) * mm, v(-31.12, 27.9) * mm, v(-30.7, 27.23) * mm, v(-30.17, 26.67) * mm]});
            skFitSpline(sketch, "E398", {"points": [v(-30.17, 26.67) * mm, v(-29.12, 25.55) * mm, v(-29.07, 25.4) * mm, v(-29.55, 24.9) * mm]});
            skFitSpline(sketch, "E399", {"points": [v(-29.55, 24.9) * mm, v(-30.1, 24.36) * mm, v(-30.96, 24.5) * mm, v(-31.6, 25.23) * mm]});
            skFitSpline(sketch, "E400", {"points": [v(-31.6, 25.23) * mm, v(-32.15, 25.85) * mm, v(-32.25, 25.88) * mm, v(-33.19, 25.74) * mm]});
            skFitSpline(sketch, "E401", {"points": [v(-33.19, 25.74) * mm, v(-34.37, 25.57) * mm, v(-35.26, 25.15) * mm, v(-35.43, 24.68) * mm]});
            skFitSpline(sketch, "E402", {"points": [v(-35.43, 24.68) * mm, v(-35.6, 24.23) * mm, v(-35.14, 24.08) * mm, v(-34.43, 24.35) * mm]});
            skFitSpline(sketch, "E403", {"points": [v(-34.43, 24.35) * mm, v(-34.1, 24.48) * mm, v(-33.54, 24.57) * mm, v(-33.15, 24.57) * mm]});
            skFitSpline(sketch, "E404", {"points": [v(-33.15, 24.57) * mm, v(-32.54, 24.57) * mm, v(-32.46, 24.5) * mm, v(-32.44, 24) * mm]});
            skFitSpline(sketch, "E405", {"points": [v(-32.44, 24) * mm, v(-32.43, 23.67) * mm, v(-32.27, 23.06) * mm, v(-32.1, 22.62) * mm]});
            skFitSpline(sketch, "E406", {"points": [v(-32.1, 22.62) * mm, v(-31.58, 21.42) * mm, v(-31.67, 20.28) * mm, v(-32.4, 18.86) * mm]});
            skFitSpline(sketch, "E407", {"points": [v(-32.4, 18.86) * mm, v(-33.14, 17.4) * mm, v(-33.17, 17.05) * mm, v(-32.63, 16.75) * mm]});
            skFitSpline(sketch, "E408", {"points": [v(-32.63, 16.75) * mm, v(-32.1, 16.47) * mm, v(-31.55, 14.82) * mm, v(-31.55, 13.54) * mm]});
            skFitSpline(sketch, "E409", {"points": [v(-31.55, 13.54) * mm, v(-31.55, 12.77) * mm, v(-31.45, 12.46) * mm, v(-31.11, 12.23) * mm]});
            skFitSpline(sketch, "E410", {"points": [v(-31.11, 12.23) * mm, v(-30.88, 12.06) * mm, v(-30.63, 11.6) * mm, v(-30.56, 11.18) * mm]});
            skFitSpline(sketch, "E411", {"points": [v(-30.56, 11.18) * mm, v(-30.46, 10.56) * mm, v(-30.52, 10.4) * mm, v(-30.91, 10.18) * mm]});
            skFitSpline(sketch, "E412", {"points": [v(-30.91, 10.18) * mm, v(-31.53, 9.85) * mm, v(-32.75, 10.1) * mm, v(-33.03, 10.6) * mm]});
            skFitSpline(sketch, "E413", {"points": [v(-33.03, 10.6) * mm, v(-33.14, 10.82) * mm, v(-33.25, 11.41) * mm, v(-33.26, 11.91) * mm]});
            skFitSpline(sketch, "E414", {"points": [v(-33.26, 11.91) * mm, v(-33.27, 12.53) * mm, v(-33.55, 13.4) * mm, v(-34.16, 14.63) * mm]});
            skFitSpline(sketch, "E415", {"points": [v(-34.16, 14.63) * mm, v(-34.97, 16.28) * mm, v(-35.1, 16.43) * mm, v(-35.72, 16.5) * mm]});
            skFitSpline(sketch, "E416", {"points": [v(-35.72, 16.5) * mm, v(-36.31, 16.55) * mm, v(-36.58, 16.38) * mm, v(-37.73, 15.23) * mm]});
            skFitSpline(sketch, "E417", {"points": [v(-37.73, 15.23) * mm, v(-38.93, 14.04) * mm, v(-39.01, 13.9) * mm, v(-38.59, 13.83) * mm]});
            skFitSpline(sketch, "E418", {"points": [v(-38.59, 13.83) * mm, v(-38.17, 13.76) * mm, v(-38.1, 13.62) * mm, v(-38.11, 12.76) * mm]});
            skFitSpline(sketch, "E419", {"points": [v(-38.11, 12.76) * mm, v(-38.12, 12.21) * mm, v(-38.4, 10.97) * mm, v(-38.75, 9.98) * mm]});
            skFitSpline(sketch, "E420", {"points": [v(-38.75, 9.98) * mm, v(-39.51, 7.8) * mm, v(-39.52, 7.37) * mm, v(-38.83, 5.2) * mm]});
            skFitSpline(sketch, "E421", {"points": [v(-38.83, 5.2) * mm, v(-38.38, 3.8) * mm, v(-38.3, 3.15) * mm, v(-38.32, 1.4) * mm]});
            skFitSpline(sketch, "E422", {"points": [v(-38.32, 1.4) * mm, v(-38.34, 0.23) * mm, v(-38.26, -1.1) * mm, v(-38.13, -1.57) * mm]});
            skFitSpline(sketch, "E423", {"points": [v(-38.13, -1.57) * mm, v(-37.77, -2.92) * mm, v(-37.86, -6.07) * mm, v(-38.34, -8.88) * mm]});
            skFitSpline(sketch, "E424", {"points": [v(-38.34, -8.88) * mm, v(-38.63, -10.58) * mm, v(-38.76, -12.12) * mm, v(-38.71, -13.3) * mm]});
            skFitSpline(sketch, "E425", {"points": [v(-38.71, -13.3) * mm, v(-38.65, -14.92) * mm, v(-38.56, -15.24) * mm, v(-37.96, -16.18) * mm]});
            skFitSpline(sketch, "E426", {"points": [v(-37.41, -20.41) * mm, v(-37.55, -24.06) * mm, v(-37.43, -24.65) * mm, v(-36.22, -26.18) * mm]});
            skFitSpline(sketch, "E427", {"points": [v(-36.22, -26.18) * mm, v(-34.5, -28.36) * mm, v(-33.66, -30.2) * mm, v(-33.66, -31.8) * mm]});
            skFitSpline(sketch, "E428", {"points": [v(-33.66, -31.8) * mm, v(-33.66, -32.5) * mm, v(-33.82, -32.8) * mm, v(-34.62, -33.66) * mm]});
            skFitSpline(sketch, "E429", {"points": [v(-34.62, -33.66) * mm, v(-35.46, -34.56) * mm, v(-35.57, -34.79) * mm, v(-35.57, -35.64) * mm]});
            skFitSpline(sketch, "E430", {"points": [v(-35.57, -35.64) * mm, v(-35.57, -36.85) * mm, v(-35.16, -37.86) * mm, v(-34.2, -38.96) * mm]});
            skFitSpline(sketch, "E431", {"points": [v(-34.2, -38.96) * mm, v(-33.8, -39.44) * mm, v(-33.28, -40.4) * mm, v(-33.04, -41.1) * mm]});
            skFitSpline(sketch, "E432", {"points": [v(-33.04, -41.1) * mm, v(-32.76, -41.93) * mm, v(-32.24, -42.8) * mm, v(-31.56, -43.59) * mm]});
            skFitSpline(sketch, "E433", {"points": [v(-31.56, -43.59) * mm, v(-29.64, -45.8) * mm, v(-29.61, -45.88) * mm, v(-29.6, -49.55) * mm]});
            skFitSpline(sketch, "E434", {"points": [v(-29.6, -49.55) * mm, v(-29.59, -51.33) * mm, v(-29.65, -53.1) * mm, v(-29.74, -53.47) * mm]});
            skFitSpline(sketch, "E435", {"points": [v(-29.74, -53.47) * mm, v(-29.87, -54.05) * mm, v(-29.78, -54.34) * mm, v(-29.2, -55.24) * mm]});
            skFitSpline(sketch, "E436", {"points": [v(-29.2, -55.24) * mm, v(-28.02, -57.1) * mm, v(-28.34, -58.63) * mm, v(-30.4, -60.92) * mm]});
            skFitSpline(sketch, "E437", {"points": [v(-30.9, -63.02) * mm, v(-30.62, -63.56) * mm, v(-29.54, -65.09) * mm, v(-28.5, -66.4) * mm]});
            skFitSpline(sketch, "E438", {"points": [v(-28.5, -66.4) * mm, v(-27.47, -67.73) * mm, v(-25.87, -70.02) * mm, v(-24.93, -71.5) * mm]});
            skFitSpline(sketch, "E439", {"points": [v(-24.93, -71.5) * mm, v(-21.66, -76.64) * mm, v(-20.53, -77.82) * mm, v(-18.3, -78.38) * mm]});
            skFitSpline(sketch, "E440", {"points": [v(-18.3, -78.38) * mm, v(-17.5, -78.58) * mm, v(-15.88, -79.13) * mm, v(-14.72, -79.6) * mm]});
            skFitSpline(sketch, "E441", {"points": [v(-14.72, -79.6) * mm, v(-13.56, -80.07) * mm, v(-12.22, -80.53) * mm, v(-11.76, -80.63) * mm]});
            skFitSpline(sketch, "E442", {"points": [v(-11.76, -80.63) * mm, v(-10.67, -80.86) * mm, v(-8.14, -80.7) * mm, v(-6.84, -80.3) * mm]});
            skFitSpline(sketch, "E443", {"points": [v(-34.5, 19.17) * mm, v(-34.65, 19.34) * mm, v(-35.11, 19.55) * mm, v(-35.54, 19.62) * mm]});
            skFitSpline(sketch, "E444", {"points": [v(-35.54, 19.62) * mm, v(-35.99, 19.7) * mm, v(-36.79, 20.15) * mm, v(-37.44, 20.68) * mm]});
            skFitSpline(sketch, "E445", {"points": [v(-37.44, 20.68) * mm, v(-38.07, 21.2) * mm, v(-38.96, 21.72) * mm, v(-39.42, 21.86) * mm]});
            skFitSpline(sketch, "E446", {"points": [v(-39.42, 21.86) * mm, v(-39.89, 22) * mm, v(-40.41, 22.34) * mm, v(-40.6, 22.6) * mm]});
            skFitSpline(sketch, "E447", {"points": [v(-40.6, 22.6) * mm, v(-40.88, 23.06) * mm, v(-40.88, 23.2) * mm, v(-40.52, 24.1) * mm]});
            skFitSpline(sketch, "E448", {"points": [v(-40.52, 24.1) * mm, v(-39.98, 25.46) * mm, v(-39.97, 28.27) * mm, v(-40.5, 29.07) * mm]});
            skFitSpline(sketch, "E449", {"points": [v(-40.5, 29.07) * mm, v(-40.94, 29.76) * mm, v(-40.96, 30.33) * mm, v(-40.55, 31.12) * mm]});
            skFitSpline(sketch, "E450", {"points": [v(-40.55, 31.12) * mm, v(-40.35, 31.5) * mm, v(-40.29, 32) * mm, v(-40.37, 32.52) * mm]});
            skFitSpline(sketch, "E451", {"points": [v(-40.37, 32.52) * mm, v(-40.49, 33.2) * mm, v(-40.43, 33.39) * mm, v(-39.97, 33.76) * mm]});
            skFitSpline(sketch, "E452", {"points": [v(-39.97, 33.76) * mm, v(-39.45, 34.2) * mm, v(-38.12, 36.16) * mm, v(-37.84, 36.9) * mm]});
            skFitSpline(sketch, "E453", {"points": [v(-37.84, 36.9) * mm, v(-37.74, 37.17) * mm, v(-37.47, 37.27) * mm, v(-36.87, 37.27) * mm]});
            skFitSpline(sketch, "E454", {"points": [v(-36.87, 37.27) * mm, v(-36.4, 37.27) * mm, v(-35.93, 37.4) * mm, v(-35.78, 37.6) * mm]});
            skFitSpline(sketch, "E455", {"points": [v(-35.78, 37.6) * mm, v(-35.64, 37.77) * mm, v(-35.2, 37.9) * mm, v(-34.82, 37.9) * mm]});
            skFitSpline(sketch, "E456", {"points": [v(-34.82, 37.9) * mm, v(-34.13, 37.9) * mm, v(-34.12, 37.9) * mm, v(-34.23, 37.12) * mm]});
            skFitSpline(sketch, "E457", {"points": [v(-34.23, 37.12) * mm, v(-34.47, 35.46) * mm, v(-34.75, 34.75) * mm, v(-35.37, 34.23) * mm]});
            skFitSpline(sketch, "E458", {"points": [v(-35.37, 34.23) * mm, v(-35.99, 33.7) * mm, v(-36, 33.67) * mm, v(-35.67, 33.16) * mm]});
            skFitSpline(sketch, "E459", {"points": [v(-35.67, 33.16) * mm, v(-34.87, 31.95) * mm, v(-36.1, 31.14) * mm, v(-37.5, 31.95) * mm]});
            skFitSpline(sketch, "E460", {"points": [v(-37.5, 31.95) * mm, v(-37.94, 32.2) * mm, v(-38.35, 32.4) * mm, v(-38.4, 32.4) * mm]});
            skFitSpline(sketch, "E461", {"points": [v(-38.4, 32.4) * mm, v(-38.63, 32.4) * mm, v(-38.23, 31.65) * mm, v(-37.44, 30.52) * mm]});
            skFitSpline(sketch, "E462", {"points": [v(-37.44, 30.52) * mm, v(-36.44, 29.1) * mm, v(-36.35, 28.09) * mm, v(-37.16, 27.33) * mm]});
            skFitSpline(sketch, "E463", {"points": [v(-37.16, 27.33) * mm, v(-37.75, 26.77) * mm, v(-37.88, 25.84) * mm, v(-37.36, 25.84) * mm]});
            skFitSpline(sketch, "E464", {"points": [v(-37.36, 25.84) * mm, v(-37.12, 25.84) * mm, v(-37.08, 25.7) * mm, v(-37.18, 25.26) * mm]});
            skFitSpline(sketch, "E465", {"points": [v(-37.18, 25.26) * mm, v(-37.37, 24.47) * mm, v(-37.66, 23.94) * mm, v(-37.9, 23.94) * mm]});
            skFitSpline(sketch, "E466", {"points": [v(-37.9, 23.94) * mm, v(-38.25, 23.94) * mm, v(-38.13, 23.18) * mm, v(-37.73, 22.82) * mm]});
            skFitSpline(sketch, "E467", {"points": [v(-37.73, 22.82) * mm, v(-37.52, 22.63) * mm, v(-36.88, 22.27) * mm, v(-36.3, 22.02) * mm]});
            skFitSpline(sketch, "E468", {"points": [v(-36.3, 22.02) * mm, v(-33.61, 20.87) * mm, v(-33.45, 20.76) * mm, v(-33.45, 20.13) * mm]});
            skFitSpline(sketch, "E469", {"points": [v(-33.45, 20.13) * mm, v(-33.45, 18.94) * mm, v(-33.94, 18.5) * mm, v(-34.5, 19.17) * mm]});
            skFitSpline(sketch, "E470", {"points": [v(-33.88, 20.11) * mm, v(-33.88, 20.2) * mm, v(-34.7, 20.65) * mm, v(-35.7, 21.1) * mm]});
            skFitSpline(sketch, "E471", {"points": [v(-35.7, 21.1) * mm, v(-38.2, 22.21) * mm, v(-38.53, 22.5) * mm, v(-38.53, 23.53) * mm]});
            skFitSpline(sketch, "E472", {"points": [v(-38.53, 23.53) * mm, v(-38.53, 23.99) * mm, v(-38.45, 24.36) * mm, v(-38.35, 24.36) * mm]});
            skFitSpline(sketch, "E473", {"points": [v(-38.35, 24.36) * mm, v(-38.26, 24.36) * mm, v(-38.08, 24.58) * mm, v(-37.96, 24.84) * mm]});
            skFitSpline(sketch, "E474", {"points": [v(-37.96, 24.84) * mm, v(-37.8, 25.2) * mm, v(-37.81, 25.39) * mm, v(-38.03, 25.6) * mm]});
            skFitSpline(sketch, "E475", {"points": [v(-38.03, 25.6) * mm, v(-38.5, 26.03) * mm, v(-38.36, 26.84) * mm, v(-37.67, 27.63) * mm]});
            skFitSpline(sketch, "E476", {"points": [v(-37.67, 27.63) * mm, v(-36.9, 28.51) * mm, v(-36.94, 28.8) * mm, v(-38.14, 30.48) * mm]});
            skFitSpline(sketch, "E477", {"points": [v(-38.14, 30.48) * mm, v(-38.63, 31.17) * mm, v(-38.96, 31.87) * mm, v(-38.96, 32.23) * mm]});
            skFitSpline(sketch, "E478", {"points": [v(-38.96, 32.23) * mm, v(-38.96, 32.75) * mm, v(-38.87, 32.83) * mm, v(-38.36, 32.83) * mm]});
            skFitSpline(sketch, "E479", {"points": [v(-38.36, 32.83) * mm, v(-38.03, 32.83) * mm, v(-37.58, 32.69) * mm, v(-37.36, 32.52) * mm]});
            skFitSpline(sketch, "E480", {"points": [v(-37.36, 32.52) * mm, v(-36.98, 32.23) * mm, v(-36, 32.07) * mm, v(-36, 32.3) * mm]});
            skFitSpline(sketch, "E481", {"points": [v(-36, 32.3) * mm, v(-36, 32.35) * mm, v(-36.15, 32.73) * mm, v(-36.35, 33.14) * mm]});
            skFitSpline(sketch, "E482", {"points": [v(-35.92, 34.57) * mm, v(-35.27, 35.14) * mm, v(-35.1, 35.46) * mm, v(-34.96, 36.38) * mm]});
            skFitSpline(sketch, "E483", {"points": [v(-34.96, 36.38) * mm, v(-34.86, 36.99) * mm, v(-34.82, 37.49) * mm, v(-34.87, 37.49) * mm]});
            skFitSpline(sketch, "E484", {"points": [v(-34.87, 37.49) * mm, v(-34.91, 37.49) * mm, v(-35.23, 37.28) * mm, v(-35.56, 37.04) * mm]});
            skFitSpline(sketch, "E485", {"points": [v(-35.56, 37.04) * mm, v(-35.96, 36.74) * mm, v(-36.36, 36.62) * mm, v(-36.72, 36.69) * mm]});
            skFitSpline(sketch, "E486", {"points": [v(-36.72, 36.69) * mm, v(-37.02, 36.75) * mm, v(-37.26, 36.72) * mm, v(-37.26, 36.64) * mm]});
            skFitSpline(sketch, "E487", {"points": [v(-37.26, 36.64) * mm, v(-37.26, 36.35) * mm, v(-39.4, 33.25) * mm, v(-39.6, 33.25) * mm]});
            skFitSpline(sketch, "E488", {"points": [v(-39.6, 33.25) * mm, v(-39.71, 33.25) * mm, v(-39.8, 32.75) * mm, v(-39.8, 32.14) * mm]});
            skFitSpline(sketch, "E489", {"points": [v(-39.8, 32.14) * mm, v(-39.81, 31.5) * mm, v(-39.95, 30.86) * mm, v(-40.13, 30.62) * mm]});
            skFitSpline(sketch, "E490", {"points": [v(-40.13, 30.62) * mm, v(-40.4, 30.26) * mm, v(-40.4, 30.15) * mm, v(-40.08, 29.67) * mm]});
            skFitSpline(sketch, "E491", {"points": [v(-40.08, 29.67) * mm, v(-39.54, 28.86) * mm, v(-39.43, 25.58) * mm, v(-39.9, 24.18) * mm]});
            skFitSpline(sketch, "E492", {"points": [v(-39.9, 24.18) * mm, v(-40.1, 23.59) * mm, v(-40.2, 23.02) * mm, v(-40.14, 22.92) * mm]});
            skFitSpline(sketch, "E493", {"points": [v(-40.14, 22.92) * mm, v(-40.08, 22.82) * mm, v(-39.57, 22.56) * mm, v(-39.02, 22.35) * mm]});
            skFitSpline(sketch, "E494", {"points": [v(-39.02, 22.35) * mm, v(-38.46, 22.15) * mm, v(-37.5, 21.56) * mm, v(-36.87, 21.05) * mm]});
            skFitSpline(sketch, "E495", {"points": [v(-36.87, 21.05) * mm, v(-36.12, 20.45) * mm, v(-35.53, 20.13) * mm, v(-35.13, 20.13) * mm]});
            skFitSpline(sketch, "E496", {"points": [v(-35.13, 20.13) * mm, v(-34.8, 20.13) * mm, v(-34.48, 20.03) * mm, v(-34.4, 19.91) * mm]});
            skFitSpline(sketch, "E497", {"points": [v(-34.4, 19.91) * mm, v(-34.26, 19.68) * mm, v(-33.88, 19.83) * mm, v(-33.88, 20.11) * mm]});
            skFitSpline(sketch, "E498", {"points": [v(-35.84, 27.25) * mm, v(-35.9, 27.35) * mm, v(-36.01, 27.96) * mm, v(-36.1, 28.6) * mm]});
            skFitSpline(sketch, "E499", {"points": [v(-36.1, 28.6) * mm, v(-36.27, 30.1) * mm, v(-35.9, 30.72) * mm, v(-35.07, 30.34) * mm]});
            skFitSpline(sketch, "E500", {"points": [v(-35.07, 30.34) * mm, v(-34.7, 30.18) * mm, v(-34.56, 29.98) * mm, v(-34.64, 29.77) * mm]});
            skFitSpline(sketch, "E501", {"points": [v(-34.64, 29.77) * mm, v(-34.74, 29.52) * mm, v(-34.61, 29.44) * mm, v(-34.1, 29.44) * mm]});
            skFitSpline(sketch, "E502", {"points": [v(-34.1, 29.44) * mm, v(-33.14, 29.44) * mm, v(-32.6, 29.1) * mm, v(-32.6, 28.48) * mm]});
            skFitSpline(sketch, "E503", {"points": [v(-32.6, 28.48) * mm, v(-32.6, 28.2) * mm, v(-32.71, 27.96) * mm, v(-32.85, 27.96) * mm]});
            skFitSpline(sketch, "E504", {"points": [v(-32.85, 27.96) * mm, v(-32.98, 27.96) * mm, v(-33.2, 27.8) * mm, v(-33.34, 27.62) * mm]});
            skFitSpline(sketch, "E505", {"points": [v(-33.34, 27.62) * mm, v(-33.62, 27.24) * mm, v(-35.65, 26.94) * mm, v(-35.84, 27.25) * mm]});
            skFitSpline(sketch, "E506", {"points": [v(-33.88, 28.07) * mm, v(-33.88, 28.24) * mm, v(-33.73, 28.38) * mm, v(-33.56, 28.38) * mm]});
            skFitSpline(sketch, "E507", {"points": [v(-33.56, 28.38) * mm, v(-33.38, 28.38) * mm, v(-33.24, 28.48) * mm, v(-33.24, 28.6) * mm]});
            skFitSpline(sketch, "E508", {"points": [v(-33.24, 28.6) * mm, v(-33.24, 28.71) * mm, v(-33.73, 28.8) * mm, v(-34.32, 28.8) * mm]});
            skFitSpline(sketch, "E509", {"points": [v(-34.32, 28.8) * mm, v(-35.4, 28.8) * mm, v(-35.4, 28.81) * mm, v(-35.31, 29.43) * mm]});
            skFitSpline(sketch, "E510", {"points": [v(-35.31, 29.43) * mm, v(-35.26, 29.77) * mm, v(-35.3, 30) * mm, v(-35.4, 29.95) * mm]});
            skFitSpline(sketch, "E511", {"points": [v(-35.4, 29.95) * mm, v(-35.6, 29.82) * mm, v(-35.62, 28.91) * mm, v(-35.44, 28.23) * mm]});
            skFitSpline(sketch, "E512", {"points": [v(-35.44, 28.23) * mm, v(-35.33, 27.85) * mm, v(-35.16, 27.75) * mm, v(-34.6, 27.75) * mm]});
            skFitSpline(sketch, "E513", {"points": [v(-34.6, 27.75) * mm, v(-34.1, 27.75) * mm, v(-33.88, 27.85) * mm, v(-33.88, 28.07) * mm]});
            skFitSpline(sketch, "E514", {"points": [v(-34.5, 30.49) * mm, v(-34.87, 31.18) * mm, v(-34.75, 31.97) * mm, v(-34.2, 32.53) * mm]});
            skFitSpline(sketch, "E515", {"points": [v(-34.2, 32.53) * mm, v(-33.9, 32.82) * mm, v(-33.66, 33.2) * mm, v(-33.66, 33.37) * mm]});
            skFitSpline(sketch, "E516", {"points": [v(-33.66, 33.37) * mm, v(-33.66, 33.54) * mm, v(-33.57, 33.68) * mm, v(-33.45, 33.68) * mm]});
            skFitSpline(sketch, "E517", {"points": [v(-33.45, 33.68) * mm, v(-33.34, 33.68) * mm, v(-33.24, 33.6) * mm, v(-33.24, 33.51) * mm]});
            skFitSpline(sketch, "E518", {"points": [v(-33.24, 33.51) * mm, v(-33.24, 33.42) * mm, v(-32.95, 33.24) * mm, v(-32.6, 33.1) * mm]});
            skFitSpline(sketch, "E519", {"points": [v(-32.6, 33.1) * mm, v(-31.72, 32.77) * mm, v(-31.8, 32.27) * mm, v(-32.94, 31.08) * mm]});
            skFitSpline(sketch, "E520", {"points": [v(-32.94, 31.08) * mm, v(-34, 29.96) * mm, v(-34.19, 29.9) * mm, v(-34.5, 30.49) * mm]});
            skFitSpline(sketch, "E521", {"points": [v(-32.6, 32.45) * mm, v(-32.6, 32.54) * mm, v(-32.75, 32.62) * mm, v(-32.92, 32.62) * mm]});
            skFitSpline(sketch, "E522", {"points": [v(-32.92, 32.62) * mm, v(-33.1, 32.62) * mm, v(-33.24, 32.53) * mm, v(-33.24, 32.43) * mm]});
            skFitSpline(sketch, "E523", {"points": [v(-33.24, 32.43) * mm, v(-33.24, 32.33) * mm, v(-33.43, 32.2) * mm, v(-33.66, 32.13) * mm]});
            skFitSpline(sketch, "E524", {"points": [v(-33.66, 32.13) * mm, v(-33.96, 32.06) * mm, v(-34.09, 31.84) * mm, v(-34.09, 31.43) * mm]});
            skFitSpline(sketch, "E525", {"points": [v(-33.35, 31.56) * mm, v(-32.94, 31.95) * mm, v(-32.6, 32.35) * mm, v(-32.6, 32.45) * mm]});
            skSolve(sketch);
        }
        {
            var Q0;
            Q0=makeQuery(id+"F0.imprint","IMPRINT",FACE,{"disambiguationData":[TD([[makeQuery(id+"F0.imprint","IMPRINT",EDGE,{"derivedFrom":sQuery(id+"F0.wireOp",EDGE,"E12")}),1.0]])]});
            var Q1;
            Q1=makeQuery(id+"F0.imprint","IMPRINT",FACE,{"disambiguationData":[TD([[makeQuery(id+"F0.imprint","IMPRINT",EDGE,{"derivedFrom":sQuery(id+"F0.wireOp",EDGE,"E26")}),1.0]])]});
            var Q2;
            Q2=makeQuery(id+"F0.imprint","IMPRINT",FACE,{"disambiguationData":[TD([[makeQuery(id+"F0.imprint","IMPRINT",EDGE,{"derivedFrom":sQuery(id+"F0.wireOp",EDGE,"E506")}),1.0]])]});
            var Q3;
            Q3=makeQuery(id+"F0.imprint","IMPRINT",FACE,{"disambiguationData":[TD([[makeQuery(id+"F0.imprint","IMPRINT",EDGE,{"derivedFrom":sQuery(id+"F0.wireOp",EDGE,"E28")}),1.0]])]});
            extrude(context, id + "F1", {"entities" : qUnion([Q0, Q1, Q2, Q3]), "depth" : 3 * mm, "offsetDistance" : 25 * mm});
        }
        {
            var Q0;
            Q0=makeQuery(id+"F1.opExtrude","CAP_FACE",FACE,{"disambiguationData":[OSD([sQuery(id+"F0.wireOp",EDGE,"E12"),sQuery(id+"F0.wireOp",EDGE,"E13"),sQuery(id+"F0.wireOp",EDGE,"E14"),sQuery(id+"F0.wireOp",EDGE,"E15"),sQuery(id+"F0.wireOp",EDGE,"E16"),sQuery(id+"F0.wireOp",EDGE,"E17"),sQuery(id+"F0.wireOp",EDGE,"E18"),sQuery(id+"F0.wireOp",EDGE,"E19"),sQuery(id+"F0.wireOp",EDGE,"E20"),sQuery(id+"F0.wireOp",EDGE,"E21"),sQuery(id+"F0.wireOp",EDGE,"E22"),sQuery(id+"F0.wireOp",EDGE,"E23"),sQuery(id+"F0.wireOp",EDGE,"E24"),sQuery(id+"F0.wireOp",EDGE,"E25"),sQuery(id+"F0.wireOp",EDGE,"E233"),sQuery(id+"F0.wireOp",EDGE,"E234"),sQuery(id+"F0.wireOp",EDGE,"E235"),sQuery(id+"F0.wireOp",EDGE,"E236"),sQuery(id+"F0.wireOp",EDGE,"E237"),sQuery(id+"F0.wireOp",EDGE,"E238"),sQuery(id+"F0.wireOp",EDGE,"E239"),sQuery(id+"F0.wireOp",EDGE,"E240"),sQuery(id+"F0.wireOp",EDGE,"E241"),sQuery(id+"F0.wireOp",EDGE,"E242"),sQuery(id+"F0.wireOp",EDGE,"E243"),sQuery(id+"F0.wireOp",EDGE,"E244"),sQuery(id+"F0.wireOp",EDGE,"E245"),sQuery(id+"F0.wireOp",EDGE,"E246"),sQuery(id+"F0.wireOp",EDGE,"E247"),sQuery(id+"F0.wireOp",EDGE,"E248"),sQuery(id+"F0.wireOp",EDGE,"E249"),sQuery(id+"F0.wireOp",EDGE,"E250"),sQuery(id+"F0.wireOp",EDGE,"E251"),sQuery(id+"F0.wireOp",EDGE,"E252"),sQuery(id+"F0.wireOp",EDGE,"E253"),sQuery(id+"F0.wireOp",EDGE,"E254"),sQuery(id+"F0.wireOp",EDGE,"E255"),sQuery(id+"F0.wireOp",EDGE,"E256"),sQuery(id+"F0.wireOp",EDGE,"E257"),sQuery(id+"F0.wireOp",EDGE,"E258"),sQuery(id+"F0.wireOp",EDGE,"E259"),sQuery(id+"F0.wireOp",EDGE,"E260"),sQuery(id+"F0.wireOp",EDGE,"E261"),sQuery(id+"F0.wireOp",EDGE,"E262"),sQuery(id+"F0.wireOp",EDGE,"E263"),sQuery(id+"F0.wireOp",EDGE,"E264"),sQuery(id+"F0.wireOp",EDGE,"E265"),sQuery(id+"F0.wireOp",EDGE,"E266"),sQuery(id+"F0.wireOp",EDGE,"E267"),sQuery(id+"F0.wireOp",EDGE,"E268"),sQuery(id+"F0.wireOp",EDGE,"E269"),sQuery(id+"F0.wireOp",EDGE,"E270"),sQuery(id+"F0.wireOp",EDGE,"E271"),sQuery(id+"F0.wireOp",EDGE,"E272"),sQuery(id+"F0.wireOp",EDGE,"E273"),sQuery(id+"F0.wireOp",EDGE,"E274"),sQuery(id+"F0.wireOp",EDGE,"E275"),sQuery(id+"F0.wireOp",EDGE,"E276"),sQuery(id+"F0.wireOp",EDGE,"E277"),sQuery(id+"F0.wireOp",EDGE,"E278"),sQuery(id+"F0.wireOp",EDGE,"E279"),sQuery(id+"F0.wireOp",EDGE,"E280"),sQuery(id+"F0.wireOp",EDGE,"E281"),sQuery(id+"F0.wireOp",EDGE,"E282"),sQuery(id+"F0.wireOp",EDGE,"E283"),sQuery(id+"F0.wireOp",EDGE,"E284"),sQuery(id+"F0.wireOp",EDGE,"E285"),sQuery(id+"F0.wireOp",EDGE,"E286"),sQuery(id+"F0.wireOp",EDGE,"E287"),sQuery(id+"F0.wireOp",EDGE,"E288"),sQuery(id+"F0.wireOp",EDGE,"E289"),sQuery(id+"F0.wireOp",EDGE,"E290"),sQuery(id+"F0.wireOp",EDGE,"E291"),sQuery(id+"F0.wireOp",EDGE,"E292"),sQuery(id+"F0.wireOp",EDGE,"E293"),sQuery(id+"F0.wireOp",EDGE,"E294"),sQuery(id+"F0.wireOp",EDGE,"E295"),sQuery(id+"F0.wireOp",EDGE,"E296"),sQuery(id+"F0.wireOp",EDGE,"E297"),sQuery(id+"F0.wireOp",EDGE,"E298"),sQuery(id+"F0.wireOp",EDGE,"E299"),sQuery(id+"F0.wireOp",EDGE,"E300"),sQuery(id+"F0.wireOp",EDGE,"E301"),sQuery(id+"F0.wireOp",EDGE,"E302"),sQuery(id+"F0.wireOp",EDGE,"E303"),sQuery(id+"F0.wireOp",EDGE,"E304"),sQuery(id+"F0.wireOp",EDGE,"E305"),sQuery(id+"F0.wireOp",EDGE,"E306"),sQuery(id+"F0.wireOp",EDGE,"E307"),sQuery(id+"F0.wireOp",EDGE,"E308"),sQuery(id+"F0.wireOp",EDGE,"E309"),sQuery(id+"F0.wireOp",EDGE,"E310"),sQuery(id+"F0.wireOp",EDGE,"E311"),sQuery(id+"F0.wireOp",EDGE,"E312"),sQuery(id+"F0.wireOp",EDGE,"E313"),sQuery(id+"F0.wireOp",EDGE,"E314"),sQuery(id+"F0.wireOp",EDGE,"E315"),sQuery(id+"F0.wireOp",EDGE,"E316"),sQuery(id+"F0.wireOp",EDGE,"E317"),sQuery(id+"F0.wireOp",EDGE,"E318"),sQuery(id+"F0.wireOp",EDGE,"E319"),sQuery(id+"F0.wireOp",EDGE,"E320"),sQuery(id+"F0.wireOp",EDGE,"E321"),sQuery(id+"F0.wireOp",EDGE,"E322"),sQuery(id+"F0.wireOp",EDGE,"E323"),sQuery(id+"F0.wireOp",EDGE,"E324"),sQuery(id+"F0.wireOp",EDGE,"E325"),sQuery(id+"F0.wireOp",EDGE,"E326"),sQuery(id+"F0.wireOp",EDGE,"E327"),sQuery(id+"F0.wireOp",EDGE,"E328"),sQuery(id+"F0.wireOp",EDGE,"E329"),sQuery(id+"F0.wireOp",EDGE,"E330"),sQuery(id+"F0.wireOp",EDGE,"E331"),sQuery(id+"F0.wireOp",EDGE,"E332"),sQuery(id+"F0.wireOp",EDGE,"E333"),sQuery(id+"F0.wireOp",EDGE,"E334"),sQuery(id+"F0.wireOp",EDGE,"E335"),sQuery(id+"F0.wireOp",EDGE,"E336"),sQuery(id+"F0.wireOp",EDGE,"E337"),sQuery(id+"F0.wireOp",EDGE,"E338"),sQuery(id+"F0.wireOp",EDGE,"E339"),sQuery(id+"F0.wireOp",EDGE,"E340"),sQuery(id+"F0.wireOp",EDGE,"E341"),sQuery(id+"F0.wireOp",EDGE,"E342"),sQuery(id+"F0.wireOp",EDGE,"E343"),sQuery(id+"F0.wireOp",EDGE,"E344"),sQuery(id+"F0.wireOp",EDGE,"E345"),sQuery(id+"F0.wireOp",EDGE,"E346"),sQuery(id+"F0.wireOp",EDGE,"E347"),sQuery(id+"F0.wireOp",EDGE,"E348"),sQuery(id+"F0.wireOp",EDGE,"E349"),sQuery(id+"F0.wireOp",EDGE,"E350"),sQuery(id+"F0.wireOp",EDGE,"E351"),sQuery(id+"F0.wireOp",EDGE,"E352"),sQuery(id+"F0.wireOp",EDGE,"E353"),sQuery(id+"F0.wireOp",EDGE,"E354"),sQuery(id+"F0.wireOp",EDGE,"E355"),sQuery(id+"F0.wireOp",EDGE,"E356"),sQuery(id+"F0.wireOp",EDGE,"E357"),sQuery(id+"F0.wireOp",EDGE,"E358"),sQuery(id+"F0.wireOp",EDGE,"E359"),sQuery(id+"F0.wireOp",EDGE,"E360"),sQuery(id+"F0.wireOp",EDGE,"E361"),sQuery(id+"F0.wireOp",EDGE,"E362"),sQuery(id+"F0.wireOp",EDGE,"E363"),sQuery(id+"F0.wireOp",EDGE,"E364"),sQuery(id+"F0.wireOp",EDGE,"E365"),sQuery(id+"F0.wireOp",EDGE,"E366"),sQuery(id+"F0.wireOp",EDGE,"E367"),sQuery(id+"F0.wireOp",EDGE,"E368"),sQuery(id+"F0.wireOp",EDGE,"E369"),sQuery(id+"F0.wireOp",EDGE,"E370"),sQuery(id+"F0.wireOp",EDGE,"E371"),sQuery(id+"F0.wireOp",EDGE,"E372"),sQuery(id+"F0.wireOp",EDGE,"E373"),sQuery(id+"F0.wireOp",EDGE,"E374"),sQuery(id+"F0.wireOp",EDGE,"E375"),sQuery(id+"F0.wireOp",EDGE,"E376"),sQuery(id+"F0.wireOp",EDGE,"E377"),sQuery(id+"F0.wireOp",EDGE,"E378"),sQuery(id+"F0.wireOp",EDGE,"E379"),sQuery(id+"F0.wireOp",EDGE,"E380"),sQuery(id+"F0.wireOp",EDGE,"E381"),sQuery(id+"F0.wireOp",EDGE,"E382"),sQuery(id+"F0.wireOp",EDGE,"E383"),sQuery(id+"F0.wireOp",EDGE,"E384"),sQuery(id+"F0.wireOp",EDGE,"E385"),sQuery(id+"F0.wireOp",EDGE,"E386"),sQuery(id+"F0.wireOp",EDGE,"E387"),sQuery(id+"F0.wireOp",EDGE,"E388"),sQuery(id+"F0.wireOp",EDGE,"E389"),sQuery(id+"F0.wireOp",EDGE,"E390"),sQuery(id+"F0.wireOp",EDGE,"E391"),sQuery(id+"F0.wireOp",EDGE,"E392"),sQuery(id+"F0.wireOp",EDGE,"E393"),sQuery(id+"F0.wireOp",EDGE,"E394"),sQuery(id+"F0.wireOp",EDGE,"E395"),sQuery(id+"F0.wireOp",EDGE,"E396"),sQuery(id+"F0.wireOp",EDGE,"E397"),sQuery(id+"F0.wireOp",EDGE,"E398"),sQuery(id+"F0.wireOp",EDGE,"E399"),sQuery(id+"F0.wireOp",EDGE,"E400"),sQuery(id+"F0.wireOp",EDGE,"E401"),sQuery(id+"F0.wireOp",EDGE,"E402"),sQuery(id+"F0.wireOp",EDGE,"E403"),sQuery(id+"F0.wireOp",EDGE,"E404"),sQuery(id+"F0.wireOp",EDGE,"E405"),sQuery(id+"F0.wireOp",EDGE,"E406"),sQuery(id+"F0.wireOp",EDGE,"E407"),sQuery(id+"F0.wireOp",EDGE,"E408"),sQuery(id+"F0.wireOp",EDGE,"E409"),sQuery(id+"F0.wireOp",EDGE,"E410"),sQuery(id+"F0.wireOp",EDGE,"E411"),sQuery(id+"F0.wireOp",EDGE,"E412"),sQuery(id+"F0.wireOp",EDGE,"E413"),sQuery(id+"F0.wireOp",EDGE,"E414"),sQuery(id+"F0.wireOp",EDGE,"E415"),sQuery(id+"F0.wireOp",EDGE,"E416"),sQuery(id+"F0.wireOp",EDGE,"E417"),sQuery(id+"F0.wireOp",EDGE,"E418"),sQuery(id+"F0.wireOp",EDGE,"E419"),sQuery(id+"F0.wireOp",EDGE,"E420"),sQuery(id+"F0.wireOp",EDGE,"E421"),sQuery(id+"F0.wireOp",EDGE,"E422"),sQuery(id+"F0.wireOp",EDGE,"E423"),sQuery(id+"F0.wireOp",EDGE,"E424"),sQuery(id+"F0.wireOp",EDGE,"E425"),sQuery(id+"F0.wireOp",EDGE,"E426"),sQuery(id+"F0.wireOp",EDGE,"E427"),sQuery(id+"F0.wireOp",EDGE,"E428"),sQuery(id+"F0.wireOp",EDGE,"E429"),sQuery(id+"F0.wireOp",EDGE,"E430"),sQuery(id+"F0.wireOp",EDGE,"E431"),sQuery(id+"F0.wireOp",EDGE,"E432"),sQuery(id+"F0.wireOp",EDGE,"E433"),sQuery(id+"F0.wireOp",EDGE,"E434"),sQuery(id+"F0.wireOp",EDGE,"E435"),sQuery(id+"F0.wireOp",EDGE,"E436"),sQuery(id+"F0.wireOp",EDGE,"E437"),sQuery(id+"F0.wireOp",EDGE,"E438"),sQuery(id+"F0.wireOp",EDGE,"E439"),sQuery(id+"F0.wireOp",EDGE,"E440"),sQuery(id+"F0.wireOp",EDGE,"E441"),sQuery(id+"F0.wireOp",EDGE,"E442")])],"isStart":false});
            var sketch = newSketch(context, id + "F2", { "sketchPlane" : qUnion([Q0])});
            skLineSegment(sketch, "E526", {"start": v(-18.12, 52.26) * mm, "end": v(-2.72, 52.26) * mm});
            skLineSegment(sketch, "E527", {"start": v(-2.72, 52.26) * mm, "end": v(-2.72, 57.25) * mm});
            skLineSegment(sketch, "E528", {"start": v(-2.72, 57.25) * mm, "end": v(9.81, 57.25) * mm});
            skLineSegment(sketch, "E529", {"start": v(9.81, 57.25) * mm, "end": v(9.81, 54.32) * mm});
            skLineSegment(sketch, "E530", {"start": v(9.81, 54.32) * mm, "end": v(15.66, 54.32) * mm});
            skLineSegment(sketch, "E531", {"start": v(15.66, 54.32) * mm, "end": v(15.66, 46.72) * mm});
            skLineSegment(sketch, "E532", {"start": v(15.66, 46.72) * mm, "end": v(7.64, 37.18) * mm});
            skLineSegment(sketch, "E533", {"start": v(7.64, 37.18) * mm, "end": v(-2.52, 37.18) * mm});
            skLineSegment(sketch, "E534", {"start": v(-2.52, 37.18) * mm, "end": v(-2.52, 39.55) * mm});
            skLineSegment(sketch, "E535", {"start": v(-2.52, 39.55) * mm, "end": v(-24.5, 39.55) * mm});
            skLineSegment(sketch, "E536", {"start": v(15.66, 51.29) * mm, "end": v(21.38, 51.29) * mm});
            skLineSegment(sketch, "E537", {"start": v(21.38, 51.29) * mm, "end": v(21.38, 60.62) * mm});
            skLineSegment(sketch, "E538", {"start": v(7.64, 37.18) * mm, "end": v(7.64, 29.75) * mm});
            skLineSegment(sketch, "E539", {"start": v(7.64, 29.75) * mm, "end": v(12.1, 22.91) * mm});
            skLineSegment(sketch, "E540", {"start": v(12.1, 22.91) * mm, "end": v(27.69, 22.91) * mm});
            skLineSegment(sketch, "E541", {"start": v(12.1, 22.91) * mm, "end": v(12.1, 16.76) * mm});
            skLineSegment(sketch, "E542", {"start": v(12.1, 16.76) * mm, "end": v(1.97, 16.76) * mm});
            skLineSegment(sketch, "E543", {"start": v(1.97, 16.76) * mm, "end": v(-2.49, 11.93) * mm});
            skLineSegment(sketch, "E544", {"start": v(-2.49, 11.93) * mm, "end": v(-2.49, -5.73) * mm});
            skLineSegment(sketch, "E545", {"start": v(-2.49, -5.73) * mm, "end": v(-11.22, -5.73) * mm});
            skLineSegment(sketch, "E546", {"start": v(-11.22, -5.73) * mm, "end": v(-11.22, -20.41) * mm});
            skLineSegment(sketch, "E547", {"start": v(-11.22, -20.41) * mm, "end": v(-37.41, -20.41) * mm});
            skLineSegment(sketch, "E548", {"start": v(12.1, 16.76) * mm, "end": v(12.1, 6.9) * mm});
            skLineSegment(sketch, "E549", {"start": v(12.1, 6.9) * mm, "end": v(20, 4.1) * mm});
            skLineSegment(sketch, "E550", {"start": v(20, 4.1) * mm, "end": v(21.49, 1.6) * mm});
            skLineSegment(sketch, "E551", {"start": v(21.49, 1.6) * mm, "end": v(30.51, 5.43) * mm});
            skLineSegment(sketch, "E552", {"start": v(-2.49, -1.8) * mm, "end": v(10.7, -1.8) * mm});
            skLineSegment(sketch, "E553", {"start": v(10.7, -1.8) * mm, "end": v(15.13, -16.6) * mm});
            skLineSegment(sketch, "E554", {"start": v(15.13, -16.6) * mm, "end": v(7.17, -21.46) * mm});
            skLineSegment(sketch, "E555", {"start": v(7.17, -21.46) * mm, "end": v(22.2, -30.75) * mm});
            skLineSegment(sketch, "E556", {"start": v(22.2, -30.75) * mm, "end": v(22.2, -20.3) * mm});
            skLineSegment(sketch, "E557", {"start": v(22.2, -20.3) * mm, "end": v(33.62, -14.84) * mm});
            skLineSegment(sketch, "E558", {"start": v(33.62, -14.84) * mm, "end": v(31.3, -9.96) * mm});
            skLineSegment(sketch, "E559", {"start": v(31.3, -9.96) * mm, "end": v(30.12, -10.51) * mm});
            skLineSegment(sketch, "E560", {"start": v(30.12, -10.51) * mm, "end": v(23.86, 2.6) * mm});
            skLineSegment(sketch, "E561", {"start": v(14.68, -26.1) * mm, "end": v(14.68, -60.19) * mm});
            skLineSegment(sketch, "E562", {"start": v(14.68, -60.19) * mm, "end": v(26.57, -60.19) * mm});
            skArc(sketch, "E563", {"start": v(37.7, -11.18) * mm, "mid": v(34.3, -11.48) * mm, "end": v(33.62, -14.84) * mm});
            skSolve(sketch);
        }
        {
            var Q0;
            Q0=makeQuery(id+"F2.imprint","IMPRINT",FACE,{"disambiguationData":[TD([[makeQuery(id+"F2.imprint","IMPRINT",EDGE,{"derivedFrom":sQuery(id+"F2.wireOp",EDGE,"E526")}),1.0]])]});
            var Q1;
            Q1=makeQuery(id+"F2.imprint","IMPRINT",FACE,{"disambiguationData":[TD([[makeQuery(id+"F2.imprint","IMPRINT",EDGE,{"derivedFrom":sQuery(id+"F2.wireOp",EDGE,"E526")}),-1.0]])]});
            var Q2;
            {var subQ2=sQuery(id+"F2.wireOp",EDGE,"E532");Q2=makeQuery(id+"F2.imprint","IMPRINT",FACE,{"disambiguationData":[TD([[makeQuery(id+"F2.imprint","IMPRINT",EDGE,{"derivedFrom":subQ2}),1.0]])]});}
            var Q3;
            Q3=makeQuery(id+"F2.imprint","IMPRINT",FACE,{"disambiguationData":[TD([[makeQuery(id+"F2.imprint","IMPRINT",EDGE,{"derivedFrom":sQuery(id+"F2.wireOp",EDGE,"E533")}),1.0]])]});
            var Q4;
            {var subQ0=sQuery(id+"F2.wireOp",EDGE,"E540");Q4=makeQuery(id+"F2.imprint","IMPRINT",FACE,{"disambiguationData":[TD([[makeQuery(id+"F2.imprint","IMPRINT",EDGE,{"derivedFrom":subQ0}),-1.0]])]});}
            var Q5;
            Q5=makeQuery(id+"F2.imprint","IMPRINT",FACE,{"disambiguationData":[TD([[makeQuery(id+"F2.imprint","IMPRINT",EDGE,{"derivedFrom":sQuery(id+"F2.wireOp",EDGE,"E542")}),1.0]])]});
            var Q6;
            {var subQ6=sQuery(id+"F2.wireOp",EDGE,"E556");Q6=makeQuery(id+"F2.imprint","IMPRINT",FACE,{"disambiguationData":[TD([[makeQuery(id+"F2.imprint","IMPRINT",EDGE,{"derivedFrom":subQ6}),-1.0]])]});}
            var Q7;
            {var subQ6=sQuery(id+"F2.wireOp",EDGE,"E545");Q7=makeQuery(id+"F2.imprint","IMPRINT",FACE,{"disambiguationData":[TD([[makeQuery(id+"F2.imprint","IMPRINT",EDGE,{"derivedFrom":subQ6}),1.0]])]});}
            extrude(context, id + "F3", {"entities" : qUnion([Q0, Q1, Q2, Q3, Q4, Q5, Q6, Q7]), "operationType" : NewBodyOperationType.REMOVE, "oppositeDirection" : true, "depth" : 25 * mm, "offsetDistance" : 25 * mm});
        }
    });
